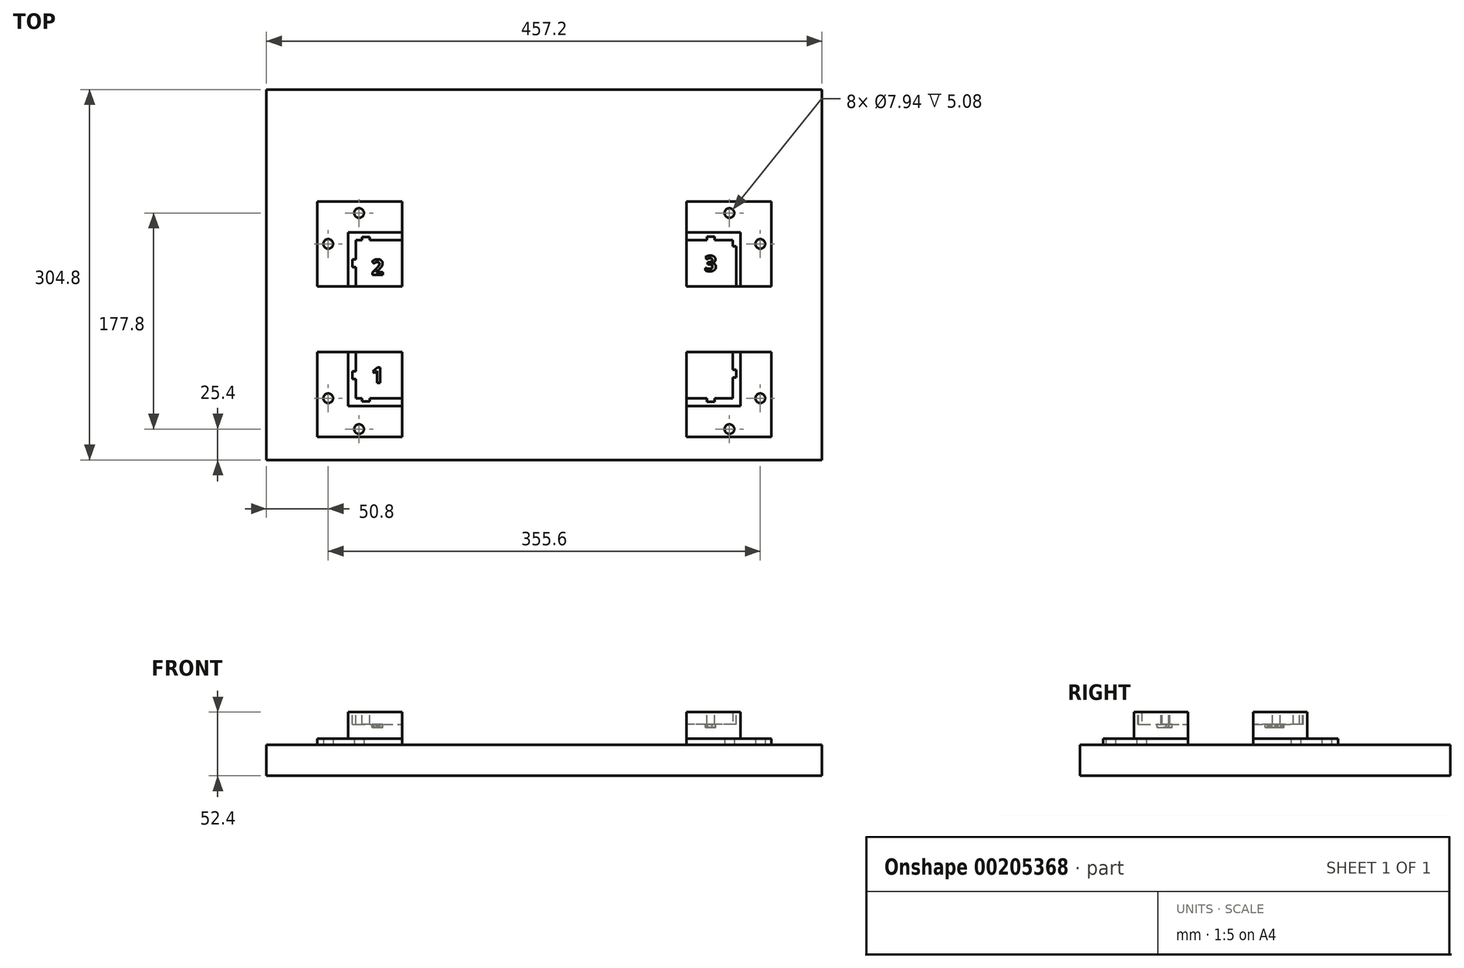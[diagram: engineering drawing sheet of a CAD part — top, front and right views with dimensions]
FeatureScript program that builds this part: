
annotation { "Feature Type Name" : "Feature", "Feature Type Description" : "" }
export const myFeature = defineFeature(function(context is Context, id is Id, definition is map)
    precondition{}
    {
        {
            var Q0;
            Q0=qCreatedBy(makeId("Top.planeOp"),FACE);
            var sketch = newSketch(context, id + "F0", { "sketchPlane" : qUnion([Q0])});
            skLineSegment(sketch, "E0.bottom", {"start": v(228.6, 152.4) * mm, "end": v(-228.6, 152.4) * mm});
            skLineSegment(sketch, "E0.top", {"start": v(228.6, -152.4) * mm, "end": v(-228.6, -152.4) * mm});
            skLineSegment(sketch, "E0.left", {"start": v(228.6, 152.4) * mm, "end": v(228.6, -152.4) * mm});
            skLineSegment(sketch, "E0.right", {"start": v(-228.6, 152.4) * mm, "end": v(-228.6, -152.4) * mm});
            skPoint(sketch, "E0.middle", {"position": v(0, 0) * mm});
            skPoint(sketch, "E1", {"position": v(-203.2, 127) * mm});
            skPoint(sketch, "E2.0.1.0", {"position": v(-203.2, 101.6) * mm});
            skPoint(sketch, "E2.0.2.0", {"position": v(-203.2, 76.2) * mm});
            skPoint(sketch, "E2.0.3.0", {"position": v(-203.2, 50.8) * mm});
            skPoint(sketch, "E2.0.4.0", {"position": v(-203.2, 25.4) * mm});
            skPoint(sketch, "E2.0.5.0", {"position": v(-203.2, 0) * mm});
            skPoint(sketch, "E2.0.6.0", {"position": v(-203.2, -25.4) * mm});
            skPoint(sketch, "E2.0.7.0", {"position": v(-203.2, -50.8) * mm});
            skPoint(sketch, "E2.0.8.0", {"position": v(-203.2, -76.2) * mm});
            skPoint(sketch, "E2.0.9.0", {"position": v(-203.2, -101.6) * mm});
            skPoint(sketch, "E2.0.10.0", {"position": v(-203.2, -127) * mm});
            skPoint(sketch, "E2.1.0.0", {"position": v(-177.8, 127) * mm});
            skPoint(sketch, "E2.1.1.0", {"position": v(-177.8, 101.6) * mm});
            skPoint(sketch, "E2.1.2.0", {"position": v(-177.8, 76.2) * mm});
            skPoint(sketch, "E2.1.3.0", {"position": v(-177.8, 50.8) * mm});
            skPoint(sketch, "E2.1.4.0", {"position": v(-177.8, 25.4) * mm});
            skPoint(sketch, "E2.1.5.0", {"position": v(-177.8, 0) * mm});
            skPoint(sketch, "E2.1.6.0", {"position": v(-177.8, -25.4) * mm});
            skPoint(sketch, "E2.1.7.0", {"position": v(-177.8, -50.8) * mm});
            skPoint(sketch, "E2.1.8.0", {"position": v(-177.8, -76.2) * mm});
            skPoint(sketch, "E2.1.9.0", {"position": v(-177.8, -101.6) * mm});
            skPoint(sketch, "E2.1.10.0", {"position": v(-177.8, -127) * mm});
            skPoint(sketch, "E2.2.0.0", {"position": v(-152.4, 127) * mm});
            skPoint(sketch, "E2.2.1.0", {"position": v(-152.4, 101.6) * mm});
            skPoint(sketch, "E2.2.2.0", {"position": v(-152.4, 76.2) * mm});
            skPoint(sketch, "E2.2.3.0", {"position": v(-152.4, 50.8) * mm});
            skPoint(sketch, "E2.2.4.0", {"position": v(-152.4, 25.4) * mm});
            skPoint(sketch, "E2.2.5.0", {"position": v(-152.4, 0) * mm});
            skPoint(sketch, "E2.2.6.0", {"position": v(-152.4, -25.4) * mm});
            skPoint(sketch, "E2.2.7.0", {"position": v(-152.4, -50.8) * mm});
            skPoint(sketch, "E2.2.8.0", {"position": v(-152.4, -76.2) * mm});
            skPoint(sketch, "E2.2.9.0", {"position": v(-152.4, -101.6) * mm});
            skPoint(sketch, "E2.2.10.0", {"position": v(-152.4, -127) * mm});
            skPoint(sketch, "E2.3.0.0", {"position": v(-127, 127) * mm});
            skPoint(sketch, "E2.3.1.0", {"position": v(-127, 101.6) * mm});
            skPoint(sketch, "E2.3.2.0", {"position": v(-127, 76.2) * mm});
            skPoint(sketch, "E2.3.3.0", {"position": v(-127, 50.8) * mm});
            skPoint(sketch, "E2.3.4.0", {"position": v(-127, 25.4) * mm});
            skPoint(sketch, "E2.3.5.0", {"position": v(-127, 0) * mm});
            skPoint(sketch, "E2.3.6.0", {"position": v(-127, -25.4) * mm});
            skPoint(sketch, "E2.3.7.0", {"position": v(-127, -50.8) * mm});
            skPoint(sketch, "E2.3.8.0", {"position": v(-127, -76.2) * mm});
            skPoint(sketch, "E2.3.9.0", {"position": v(-127, -101.6) * mm});
            skPoint(sketch, "E2.3.10.0", {"position": v(-127, -127) * mm});
            skPoint(sketch, "E2.4.0.0", {"position": v(-101.6, 127) * mm});
            skPoint(sketch, "E2.4.1.0", {"position": v(-101.6, 101.6) * mm});
            skPoint(sketch, "E2.4.2.0", {"position": v(-101.6, 76.2) * mm});
            skPoint(sketch, "E2.4.3.0", {"position": v(-101.6, 50.8) * mm});
            skPoint(sketch, "E2.4.4.0", {"position": v(-101.6, 25.4) * mm});
            skPoint(sketch, "E2.4.5.0", {"position": v(-101.6, 0) * mm});
            skPoint(sketch, "E2.4.6.0", {"position": v(-101.6, -25.4) * mm});
            skPoint(sketch, "E2.4.7.0", {"position": v(-101.6, -50.8) * mm});
            skPoint(sketch, "E2.4.8.0", {"position": v(-101.6, -76.2) * mm});
            skPoint(sketch, "E2.4.9.0", {"position": v(-101.6, -101.6) * mm});
            skPoint(sketch, "E2.4.10.0", {"position": v(-101.6, -127) * mm});
            skPoint(sketch, "E2.5.0.0", {"position": v(-76.2, 127) * mm});
            skPoint(sketch, "E2.5.1.0", {"position": v(-76.2, 101.6) * mm});
            skPoint(sketch, "E2.5.2.0", {"position": v(-76.2, 76.2) * mm});
            skPoint(sketch, "E2.5.3.0", {"position": v(-76.2, 50.8) * mm});
            skPoint(sketch, "E2.5.4.0", {"position": v(-76.2, 25.4) * mm});
            skPoint(sketch, "E2.5.5.0", {"position": v(-76.2, 0) * mm});
            skPoint(sketch, "E2.5.6.0", {"position": v(-76.2, -25.4) * mm});
            skPoint(sketch, "E2.5.7.0", {"position": v(-76.2, -50.8) * mm});
            skPoint(sketch, "E2.5.8.0", {"position": v(-76.2, -76.2) * mm});
            skPoint(sketch, "E2.5.9.0", {"position": v(-76.2, -101.6) * mm});
            skPoint(sketch, "E2.5.10.0", {"position": v(-76.2, -127) * mm});
            skPoint(sketch, "E2.6.0.0", {"position": v(-50.8, 127) * mm});
            skPoint(sketch, "E2.6.1.0", {"position": v(-50.8, 101.6) * mm});
            skPoint(sketch, "E2.6.2.0", {"position": v(-50.8, 76.2) * mm});
            skPoint(sketch, "E2.6.3.0", {"position": v(-50.8, 50.8) * mm});
            skPoint(sketch, "E2.6.4.0", {"position": v(-50.8, 25.4) * mm});
            skPoint(sketch, "E2.6.5.0", {"position": v(-50.8, 0) * mm});
            skPoint(sketch, "E2.6.6.0", {"position": v(-50.8, -25.4) * mm});
            skPoint(sketch, "E2.6.7.0", {"position": v(-50.8, -50.8) * mm});
            skPoint(sketch, "E2.6.8.0", {"position": v(-50.8, -76.2) * mm});
            skPoint(sketch, "E2.6.9.0", {"position": v(-50.8, -101.6) * mm});
            skPoint(sketch, "E2.6.10.0", {"position": v(-50.8, -127) * mm});
            skPoint(sketch, "E2.7.0.0", {"position": v(-25.4, 127) * mm});
            skPoint(sketch, "E2.7.1.0", {"position": v(-25.4, 101.6) * mm});
            skPoint(sketch, "E2.7.2.0", {"position": v(-25.4, 76.2) * mm});
            skPoint(sketch, "E2.7.3.0", {"position": v(-25.4, 50.8) * mm});
            skPoint(sketch, "E2.7.4.0", {"position": v(-25.4, 25.4) * mm});
            skPoint(sketch, "E2.7.5.0", {"position": v(-25.4, 0) * mm});
            skPoint(sketch, "E2.7.6.0", {"position": v(-25.4, -25.4) * mm});
            skPoint(sketch, "E2.7.7.0", {"position": v(-25.4, -50.8) * mm});
            skPoint(sketch, "E2.7.8.0", {"position": v(-25.4, -76.2) * mm});
            skPoint(sketch, "E2.7.9.0", {"position": v(-25.4, -101.6) * mm});
            skPoint(sketch, "E2.7.10.0", {"position": v(-25.4, -127) * mm});
            skPoint(sketch, "E2.8.0.0", {"position": v(0, 127) * mm});
            skPoint(sketch, "E2.8.1.0", {"position": v(0, 101.6) * mm});
            skPoint(sketch, "E2.8.2.0", {"position": v(0, 76.2) * mm});
            skPoint(sketch, "E2.8.3.0", {"position": v(0, 50.8) * mm});
            skPoint(sketch, "E2.8.4.0", {"position": v(0, 25.4) * mm});
            skPoint(sketch, "E2.8.6.0", {"position": v(0, -25.4) * mm});
            skPoint(sketch, "E2.8.7.0", {"position": v(0, -50.8) * mm});
            skPoint(sketch, "E2.8.8.0", {"position": v(0, -76.2) * mm});
            skPoint(sketch, "E2.8.9.0", {"position": v(0, -101.6) * mm});
            skPoint(sketch, "E2.8.10.0", {"position": v(0, -127) * mm});
            skPoint(sketch, "E2.9.0.0", {"position": v(25.4, 127) * mm});
            skPoint(sketch, "E2.9.1.0", {"position": v(25.4, 101.6) * mm});
            skPoint(sketch, "E2.9.2.0", {"position": v(25.4, 76.2) * mm});
            skPoint(sketch, "E2.9.3.0", {"position": v(25.4, 50.8) * mm});
            skPoint(sketch, "E2.9.4.0", {"position": v(25.4, 25.4) * mm});
            skPoint(sketch, "E2.9.5.0", {"position": v(25.4, 0) * mm});
            skPoint(sketch, "E2.9.6.0", {"position": v(25.4, -25.4) * mm});
            skPoint(sketch, "E2.9.7.0", {"position": v(25.4, -50.8) * mm});
            skPoint(sketch, "E2.9.8.0", {"position": v(25.4, -76.2) * mm});
            skPoint(sketch, "E2.9.9.0", {"position": v(25.4, -101.6) * mm});
            skPoint(sketch, "E2.9.10.0", {"position": v(25.4, -127) * mm});
            skPoint(sketch, "E2.10.0.0", {"position": v(50.8, 127) * mm});
            skPoint(sketch, "E2.10.1.0", {"position": v(50.8, 101.6) * mm});
            skPoint(sketch, "E2.10.2.0", {"position": v(50.8, 76.2) * mm});
            skPoint(sketch, "E2.10.3.0", {"position": v(50.8, 50.8) * mm});
            skPoint(sketch, "E2.10.4.0", {"position": v(50.8, 25.4) * mm});
            skPoint(sketch, "E2.10.5.0", {"position": v(50.8, 0) * mm});
            skPoint(sketch, "E2.10.6.0", {"position": v(50.8, -25.4) * mm});
            skPoint(sketch, "E2.10.7.0", {"position": v(50.8, -50.8) * mm});
            skPoint(sketch, "E2.10.8.0", {"position": v(50.8, -76.2) * mm});
            skPoint(sketch, "E2.10.9.0", {"position": v(50.8, -101.6) * mm});
            skPoint(sketch, "E2.10.10.0", {"position": v(50.8, -127) * mm});
            skPoint(sketch, "E2.11.0.0", {"position": v(76.2, 127) * mm});
            skPoint(sketch, "E2.11.1.0", {"position": v(76.2, 101.6) * mm});
            skPoint(sketch, "E2.11.2.0", {"position": v(76.2, 76.2) * mm});
            skPoint(sketch, "E2.11.3.0", {"position": v(76.2, 50.8) * mm});
            skPoint(sketch, "E2.11.4.0", {"position": v(76.2, 25.4) * mm});
            skPoint(sketch, "E2.11.5.0", {"position": v(76.2, 0) * mm});
            skPoint(sketch, "E2.11.6.0", {"position": v(76.2, -25.4) * mm});
            skPoint(sketch, "E2.11.7.0", {"position": v(76.2, -50.8) * mm});
            skPoint(sketch, "E2.11.8.0", {"position": v(76.2, -76.2) * mm});
            skPoint(sketch, "E2.11.9.0", {"position": v(76.2, -101.6) * mm});
            skPoint(sketch, "E2.11.10.0", {"position": v(76.2, -127) * mm});
            skPoint(sketch, "E2.12.0.0", {"position": v(101.6, 127) * mm});
            skPoint(sketch, "E2.12.1.0", {"position": v(101.6, 101.6) * mm});
            skPoint(sketch, "E2.12.2.0", {"position": v(101.6, 76.2) * mm});
            skPoint(sketch, "E2.12.3.0", {"position": v(101.6, 50.8) * mm});
            skPoint(sketch, "E2.12.4.0", {"position": v(101.6, 25.4) * mm});
            skPoint(sketch, "E2.12.5.0", {"position": v(101.6, 0) * mm});
            skPoint(sketch, "E2.12.6.0", {"position": v(101.6, -25.4) * mm});
            skPoint(sketch, "E2.12.7.0", {"position": v(101.6, -50.8) * mm});
            skPoint(sketch, "E2.12.8.0", {"position": v(101.6, -76.2) * mm});
            skPoint(sketch, "E2.12.9.0", {"position": v(101.6, -101.6) * mm});
            skPoint(sketch, "E2.12.10.0", {"position": v(101.6, -127) * mm});
            skPoint(sketch, "E2.13.0.0", {"position": v(127, 127) * mm});
            skPoint(sketch, "E2.13.1.0", {"position": v(127, 101.6) * mm});
            skPoint(sketch, "E2.13.2.0", {"position": v(127, 76.2) * mm});
            skPoint(sketch, "E2.13.3.0", {"position": v(127, 50.8) * mm});
            skPoint(sketch, "E2.13.4.0", {"position": v(127, 25.4) * mm});
            skPoint(sketch, "E2.13.5.0", {"position": v(127, 0) * mm});
            skPoint(sketch, "E2.13.6.0", {"position": v(127, -25.4) * mm});
            skPoint(sketch, "E2.13.7.0", {"position": v(127, -50.8) * mm});
            skPoint(sketch, "E2.13.8.0", {"position": v(127, -76.2) * mm});
            skPoint(sketch, "E2.13.9.0", {"position": v(127, -101.6) * mm});
            skPoint(sketch, "E2.13.10.0", {"position": v(127, -127) * mm});
            skPoint(sketch, "E2.14.0.0", {"position": v(152.4, 127) * mm});
            skPoint(sketch, "E2.14.1.0", {"position": v(152.4, 101.6) * mm});
            skPoint(sketch, "E2.14.2.0", {"position": v(152.4, 76.2) * mm});
            skPoint(sketch, "E2.14.3.0", {"position": v(152.4, 50.8) * mm});
            skPoint(sketch, "E2.14.4.0", {"position": v(152.4, 25.4) * mm});
            skPoint(sketch, "E2.14.5.0", {"position": v(152.4, 0) * mm});
            skPoint(sketch, "E2.14.6.0", {"position": v(152.4, -25.4) * mm});
            skPoint(sketch, "E2.14.7.0", {"position": v(152.4, -50.8) * mm});
            skPoint(sketch, "E2.14.8.0", {"position": v(152.4, -76.2) * mm});
            skPoint(sketch, "E2.14.9.0", {"position": v(152.4, -101.6) * mm});
            skPoint(sketch, "E2.14.10.0", {"position": v(152.4, -127) * mm});
            skPoint(sketch, "E2.15.0.0", {"position": v(177.8, 127) * mm});
            skPoint(sketch, "E2.15.1.0", {"position": v(177.8, 101.6) * mm});
            skPoint(sketch, "E2.15.2.0", {"position": v(177.8, 76.2) * mm});
            skPoint(sketch, "E2.15.3.0", {"position": v(177.8, 50.8) * mm});
            skPoint(sketch, "E2.15.4.0", {"position": v(177.8, 25.4) * mm});
            skPoint(sketch, "E2.15.5.0", {"position": v(177.8, 0) * mm});
            skPoint(sketch, "E2.15.6.0", {"position": v(177.8, -25.4) * mm});
            skPoint(sketch, "E2.15.7.0", {"position": v(177.8, -50.8) * mm});
            skPoint(sketch, "E2.15.8.0", {"position": v(177.8, -76.2) * mm});
            skPoint(sketch, "E2.15.9.0", {"position": v(177.8, -101.6) * mm});
            skPoint(sketch, "E2.15.10.0", {"position": v(177.8, -127) * mm});
            skPoint(sketch, "E2.16.0.0", {"position": v(203.2, 127) * mm});
            skPoint(sketch, "E2.16.1.0", {"position": v(203.2, 101.6) * mm});
            skPoint(sketch, "E2.16.2.0", {"position": v(203.2, 76.2) * mm});
            skPoint(sketch, "E2.16.3.0", {"position": v(203.2, 50.8) * mm});
            skPoint(sketch, "E2.16.4.0", {"position": v(203.2, 25.4) * mm});
            skPoint(sketch, "E2.16.5.0", {"position": v(203.2, 0) * mm});
            skPoint(sketch, "E2.16.6.0", {"position": v(203.2, -25.4) * mm});
            skPoint(sketch, "E2.16.7.0", {"position": v(203.2, -50.8) * mm});
            skPoint(sketch, "E2.16.8.0", {"position": v(203.2, -76.2) * mm});
            skPoint(sketch, "E2.16.9.0", {"position": v(203.2, -101.6) * mm});
            skPoint(sketch, "E2.16.10.0", {"position": v(203.2, -127) * mm});
            skLineSegment(sketch, "E2.direction1", {"start": v(-203.2, 127) * mm, "end": v(-177.8, 127) * mm, "construction": true});
            skLineSegment(sketch, "E2.direction2", {"start": v(-203.2, 127) * mm, "end": v(-203.2, 101.6) * mm, "construction": true});
            skCircle(sketch, "E3", {"center": v(-203.2, 127) * mm, "radius": 3.18 * mm, "construction": true});
            skCircle(sketch, "E4.0.1.0", {"center": v(-203.2, 101.6) * mm, "radius": 3.18 * mm, "construction": true});
            skCircle(sketch, "E4.0.2.0", {"center": v(-203.2, 76.2) * mm, "radius": 3.18 * mm, "construction": true});
            skCircle(sketch, "E4.0.3.0", {"center": v(-203.2, 50.8) * mm, "radius": 3.18 * mm, "construction": true});
            skCircle(sketch, "E4.0.4.0", {"center": v(-203.2, 25.4) * mm, "radius": 3.18 * mm, "construction": true});
            skCircle(sketch, "E4.0.5.0", {"center": v(-203.2, 0) * mm, "radius": 3.18 * mm, "construction": true});
            skCircle(sketch, "E4.0.6.0", {"center": v(-203.2, -25.4) * mm, "radius": 3.18 * mm, "construction": true});
            skCircle(sketch, "E4.0.7.0", {"center": v(-203.2, -50.8) * mm, "radius": 3.18 * mm, "construction": true});
            skCircle(sketch, "E4.0.8.0", {"center": v(-203.2, -76.2) * mm, "radius": 3.18 * mm, "construction": true});
            skCircle(sketch, "E4.0.9.0", {"center": v(-203.2, -101.6) * mm, "radius": 3.18 * mm, "construction": true});
            skCircle(sketch, "E4.0.10.0", {"center": v(-203.2, -127) * mm, "radius": 3.18 * mm, "construction": true});
            skCircle(sketch, "E4.1.0.0", {"center": v(-177.8, 127) * mm, "radius": 3.18 * mm, "construction": true});
            skCircle(sketch, "E4.1.1.0", {"center": v(-177.8, 101.6) * mm, "radius": 3.18 * mm, "construction": true});
            skCircle(sketch, "E4.1.2.0", {"center": v(-177.8, 76.2) * mm, "radius": 3.18 * mm, "construction": true});
            skCircle(sketch, "E4.1.3.0", {"center": v(-177.8, 50.8) * mm, "radius": 3.18 * mm, "construction": true});
            skCircle(sketch, "E4.1.4.0", {"center": v(-177.8, 25.4) * mm, "radius": 3.18 * mm, "construction": true});
            skCircle(sketch, "E4.1.5.0", {"center": v(-177.8, 0) * mm, "radius": 3.18 * mm, "construction": true});
            skCircle(sketch, "E4.1.6.0", {"center": v(-177.8, -25.4) * mm, "radius": 3.18 * mm, "construction": true});
            skCircle(sketch, "E4.1.7.0", {"center": v(-177.8, -50.8) * mm, "radius": 3.18 * mm, "construction": true});
            skCircle(sketch, "E4.1.8.0", {"center": v(-177.8, -76.2) * mm, "radius": 3.18 * mm, "construction": true});
            skCircle(sketch, "E4.1.9.0", {"center": v(-177.8, -101.6) * mm, "radius": 3.18 * mm, "construction": true});
            skCircle(sketch, "E4.1.10.0", {"center": v(-177.8, -127) * mm, "radius": 3.18 * mm, "construction": true});
            skCircle(sketch, "E4.2.0.0", {"center": v(-152.4, 127) * mm, "radius": 3.18 * mm, "construction": true});
            skCircle(sketch, "E4.2.1.0", {"center": v(-152.4, 101.6) * mm, "radius": 3.18 * mm, "construction": true});
            skCircle(sketch, "E4.2.2.0", {"center": v(-152.4, 76.2) * mm, "radius": 3.18 * mm, "construction": true});
            skCircle(sketch, "E4.2.3.0", {"center": v(-152.4, 50.8) * mm, "radius": 3.18 * mm, "construction": true});
            skCircle(sketch, "E4.2.4.0", {"center": v(-152.4, 25.4) * mm, "radius": 3.18 * mm, "construction": true});
            skCircle(sketch, "E4.2.5.0", {"center": v(-152.4, 0) * mm, "radius": 3.18 * mm, "construction": true});
            skCircle(sketch, "E4.2.6.0", {"center": v(-152.4, -25.4) * mm, "radius": 3.18 * mm, "construction": true});
            skCircle(sketch, "E4.2.7.0", {"center": v(-152.4, -50.8) * mm, "radius": 3.18 * mm, "construction": true});
            skCircle(sketch, "E4.2.8.0", {"center": v(-152.4, -76.2) * mm, "radius": 3.18 * mm, "construction": true});
            skCircle(sketch, "E4.2.9.0", {"center": v(-152.4, -101.6) * mm, "radius": 3.18 * mm, "construction": true});
            skCircle(sketch, "E4.2.10.0", {"center": v(-152.4, -127) * mm, "radius": 3.18 * mm, "construction": true});
            skCircle(sketch, "E4.3.0.0", {"center": v(-127, 127) * mm, "radius": 3.18 * mm, "construction": true});
            skCircle(sketch, "E4.3.1.0", {"center": v(-127, 101.6) * mm, "radius": 3.18 * mm, "construction": true});
            skCircle(sketch, "E4.3.2.0", {"center": v(-127, 76.2) * mm, "radius": 3.18 * mm, "construction": true});
            skCircle(sketch, "E4.3.3.0", {"center": v(-127, 50.8) * mm, "radius": 3.18 * mm, "construction": true});
            skCircle(sketch, "E4.3.4.0", {"center": v(-127, 25.4) * mm, "radius": 3.18 * mm, "construction": true});
            skCircle(sketch, "E4.3.5.0", {"center": v(-127, 0) * mm, "radius": 3.18 * mm, "construction": true});
            skCircle(sketch, "E4.3.6.0", {"center": v(-127, -25.4) * mm, "radius": 3.18 * mm, "construction": true});
            skCircle(sketch, "E4.3.7.0", {"center": v(-127, -50.8) * mm, "radius": 3.18 * mm, "construction": true});
            skCircle(sketch, "E4.3.8.0", {"center": v(-127, -76.2) * mm, "radius": 3.18 * mm, "construction": true});
            skCircle(sketch, "E4.3.9.0", {"center": v(-127, -101.6) * mm, "radius": 3.18 * mm, "construction": true});
            skCircle(sketch, "E4.3.10.0", {"center": v(-127, -127) * mm, "radius": 3.18 * mm, "construction": true});
            skCircle(sketch, "E4.4.0.0", {"center": v(-101.6, 127) * mm, "radius": 3.18 * mm, "construction": true});
            skCircle(sketch, "E4.4.1.0", {"center": v(-101.6, 101.6) * mm, "radius": 3.18 * mm, "construction": true});
            skCircle(sketch, "E4.4.2.0", {"center": v(-101.6, 76.2) * mm, "radius": 3.18 * mm, "construction": true});
            skCircle(sketch, "E4.4.3.0", {"center": v(-101.6, 50.8) * mm, "radius": 3.18 * mm, "construction": true});
            skCircle(sketch, "E4.4.4.0", {"center": v(-101.6, 25.4) * mm, "radius": 3.18 * mm, "construction": true});
            skCircle(sketch, "E4.4.5.0", {"center": v(-101.6, 0) * mm, "radius": 3.18 * mm, "construction": true});
            skCircle(sketch, "E4.4.6.0", {"center": v(-101.6, -25.4) * mm, "radius": 3.18 * mm, "construction": true});
            skCircle(sketch, "E4.4.7.0", {"center": v(-101.6, -50.8) * mm, "radius": 3.18 * mm, "construction": true});
            skCircle(sketch, "E4.4.8.0", {"center": v(-101.6, -76.2) * mm, "radius": 3.18 * mm, "construction": true});
            skCircle(sketch, "E4.4.9.0", {"center": v(-101.6, -101.6) * mm, "radius": 3.18 * mm, "construction": true});
            skCircle(sketch, "E4.4.10.0", {"center": v(-101.6, -127) * mm, "radius": 3.18 * mm, "construction": true});
            skCircle(sketch, "E4.5.0.0", {"center": v(-76.2, 127) * mm, "radius": 3.18 * mm, "construction": true});
            skCircle(sketch, "E4.5.1.0", {"center": v(-76.2, 101.6) * mm, "radius": 3.18 * mm, "construction": true});
            skCircle(sketch, "E4.5.2.0", {"center": v(-76.2, 76.2) * mm, "radius": 3.18 * mm, "construction": true});
            skCircle(sketch, "E4.5.3.0", {"center": v(-76.2, 50.8) * mm, "radius": 3.18 * mm, "construction": true});
            skCircle(sketch, "E4.5.4.0", {"center": v(-76.2, 25.4) * mm, "radius": 3.18 * mm, "construction": true});
            skCircle(sketch, "E4.5.5.0", {"center": v(-76.2, 0) * mm, "radius": 3.18 * mm, "construction": true});
            skCircle(sketch, "E4.5.6.0", {"center": v(-76.2, -25.4) * mm, "radius": 3.18 * mm, "construction": true});
            skCircle(sketch, "E4.5.7.0", {"center": v(-76.2, -50.8) * mm, "radius": 3.18 * mm, "construction": true});
            skCircle(sketch, "E4.5.8.0", {"center": v(-76.2, -76.2) * mm, "radius": 3.18 * mm, "construction": true});
            skCircle(sketch, "E4.5.9.0", {"center": v(-76.2, -101.6) * mm, "radius": 3.18 * mm, "construction": true});
            skCircle(sketch, "E4.5.10.0", {"center": v(-76.2, -127) * mm, "radius": 3.18 * mm, "construction": true});
            skCircle(sketch, "E4.6.0.0", {"center": v(-50.8, 127) * mm, "radius": 3.18 * mm, "construction": true});
            skCircle(sketch, "E4.6.1.0", {"center": v(-50.8, 101.6) * mm, "radius": 3.18 * mm, "construction": true});
            skCircle(sketch, "E4.6.2.0", {"center": v(-50.8, 76.2) * mm, "radius": 3.18 * mm, "construction": true});
            skCircle(sketch, "E4.6.3.0", {"center": v(-50.8, 50.8) * mm, "radius": 3.18 * mm, "construction": true});
            skCircle(sketch, "E4.6.4.0", {"center": v(-50.8, 25.4) * mm, "radius": 3.18 * mm, "construction": true});
            skCircle(sketch, "E4.6.5.0", {"center": v(-50.8, 0) * mm, "radius": 3.18 * mm, "construction": true});
            skCircle(sketch, "E4.6.6.0", {"center": v(-50.8, -25.4) * mm, "radius": 3.18 * mm, "construction": true});
            skCircle(sketch, "E4.6.7.0", {"center": v(-50.8, -50.8) * mm, "radius": 3.18 * mm, "construction": true});
            skCircle(sketch, "E4.6.8.0", {"center": v(-50.8, -76.2) * mm, "radius": 3.18 * mm, "construction": true});
            skCircle(sketch, "E4.6.9.0", {"center": v(-50.8, -101.6) * mm, "radius": 3.18 * mm, "construction": true});
            skCircle(sketch, "E4.6.10.0", {"center": v(-50.8, -127) * mm, "radius": 3.18 * mm, "construction": true});
            skCircle(sketch, "E4.7.0.0", {"center": v(-25.4, 127) * mm, "radius": 3.18 * mm, "construction": true});
            skCircle(sketch, "E4.7.1.0", {"center": v(-25.4, 101.6) * mm, "radius": 3.18 * mm, "construction": true});
            skCircle(sketch, "E4.7.2.0", {"center": v(-25.4, 76.2) * mm, "radius": 3.18 * mm, "construction": true});
            skCircle(sketch, "E4.7.3.0", {"center": v(-25.4, 50.8) * mm, "radius": 3.18 * mm, "construction": true});
            skCircle(sketch, "E4.7.4.0", {"center": v(-25.4, 25.4) * mm, "radius": 3.18 * mm, "construction": true});
            skCircle(sketch, "E4.7.5.0", {"center": v(-25.4, 0) * mm, "radius": 3.18 * mm, "construction": true});
            skCircle(sketch, "E4.7.6.0", {"center": v(-25.4, -25.4) * mm, "radius": 3.18 * mm, "construction": true});
            skCircle(sketch, "E4.7.7.0", {"center": v(-25.4, -50.8) * mm, "radius": 3.18 * mm, "construction": true});
            skCircle(sketch, "E4.7.8.0", {"center": v(-25.4, -76.2) * mm, "radius": 3.18 * mm, "construction": true});
            skCircle(sketch, "E4.7.9.0", {"center": v(-25.4, -101.6) * mm, "radius": 3.18 * mm, "construction": true});
            skCircle(sketch, "E4.7.10.0", {"center": v(-25.4, -127) * mm, "radius": 3.18 * mm, "construction": true});
            skCircle(sketch, "E4.8.0.0", {"center": v(0, 127) * mm, "radius": 3.18 * mm, "construction": true});
            skCircle(sketch, "E4.8.1.0", {"center": v(0, 101.6) * mm, "radius": 3.18 * mm, "construction": true});
            skCircle(sketch, "E4.8.2.0", {"center": v(0, 76.2) * mm, "radius": 3.18 * mm, "construction": true});
            skCircle(sketch, "E4.8.3.0", {"center": v(0, 50.8) * mm, "radius": 3.18 * mm, "construction": true});
            skCircle(sketch, "E4.8.4.0", {"center": v(0, 25.4) * mm, "radius": 3.18 * mm, "construction": true});
            skCircle(sketch, "E4.8.5.0", {"center": v(0, 0) * mm, "radius": 3.18 * mm, "construction": true});
            skCircle(sketch, "E4.8.6.0", {"center": v(0, -25.4) * mm, "radius": 3.18 * mm, "construction": true});
            skCircle(sketch, "E4.8.7.0", {"center": v(0, -50.8) * mm, "radius": 3.18 * mm, "construction": true});
            skCircle(sketch, "E4.8.8.0", {"center": v(0, -76.2) * mm, "radius": 3.18 * mm, "construction": true});
            skCircle(sketch, "E4.8.9.0", {"center": v(0, -101.6) * mm, "radius": 3.18 * mm, "construction": true});
            skCircle(sketch, "E4.8.10.0", {"center": v(0, -127) * mm, "radius": 3.18 * mm, "construction": true});
            skCircle(sketch, "E4.9.0.0", {"center": v(25.4, 127) * mm, "radius": 3.18 * mm, "construction": true});
            skCircle(sketch, "E4.9.1.0", {"center": v(25.4, 101.6) * mm, "radius": 3.18 * mm, "construction": true});
            skCircle(sketch, "E4.9.2.0", {"center": v(25.4, 76.2) * mm, "radius": 3.18 * mm, "construction": true});
            skCircle(sketch, "E4.9.3.0", {"center": v(25.4, 50.8) * mm, "radius": 3.18 * mm, "construction": true});
            skCircle(sketch, "E4.9.4.0", {"center": v(25.4, 25.4) * mm, "radius": 3.18 * mm, "construction": true});
            skCircle(sketch, "E4.9.5.0", {"center": v(25.4, 0) * mm, "radius": 3.18 * mm, "construction": true});
            skCircle(sketch, "E4.9.6.0", {"center": v(25.4, -25.4) * mm, "radius": 3.18 * mm, "construction": true});
            skCircle(sketch, "E4.9.7.0", {"center": v(25.4, -50.8) * mm, "radius": 3.18 * mm, "construction": true});
            skCircle(sketch, "E4.9.8.0", {"center": v(25.4, -76.2) * mm, "radius": 3.18 * mm, "construction": true});
            skCircle(sketch, "E4.9.9.0", {"center": v(25.4, -101.6) * mm, "radius": 3.18 * mm, "construction": true});
            skCircle(sketch, "E4.9.10.0", {"center": v(25.4, -127) * mm, "radius": 3.18 * mm, "construction": true});
            skCircle(sketch, "E4.10.0.0", {"center": v(50.8, 127) * mm, "radius": 3.18 * mm, "construction": true});
            skCircle(sketch, "E4.10.1.0", {"center": v(50.8, 101.6) * mm, "radius": 3.18 * mm, "construction": true});
            skCircle(sketch, "E4.10.2.0", {"center": v(50.8, 76.2) * mm, "radius": 3.18 * mm, "construction": true});
            skCircle(sketch, "E4.10.3.0", {"center": v(50.8, 50.8) * mm, "radius": 3.18 * mm, "construction": true});
            skCircle(sketch, "E4.10.4.0", {"center": v(50.8, 25.4) * mm, "radius": 3.18 * mm, "construction": true});
            skCircle(sketch, "E4.10.5.0", {"center": v(50.8, 0) * mm, "radius": 3.18 * mm, "construction": true});
            skCircle(sketch, "E4.10.6.0", {"center": v(50.8, -25.4) * mm, "radius": 3.18 * mm, "construction": true});
            skCircle(sketch, "E4.10.7.0", {"center": v(50.8, -50.8) * mm, "radius": 3.18 * mm, "construction": true});
            skCircle(sketch, "E4.10.8.0", {"center": v(50.8, -76.2) * mm, "radius": 3.18 * mm, "construction": true});
            skCircle(sketch, "E4.10.9.0", {"center": v(50.8, -101.6) * mm, "radius": 3.18 * mm, "construction": true});
            skCircle(sketch, "E4.10.10.0", {"center": v(50.8, -127) * mm, "radius": 3.18 * mm, "construction": true});
            skCircle(sketch, "E4.11.0.0", {"center": v(76.2, 127) * mm, "radius": 3.18 * mm, "construction": true});
            skCircle(sketch, "E4.11.1.0", {"center": v(76.2, 101.6) * mm, "radius": 3.18 * mm, "construction": true});
            skCircle(sketch, "E4.11.2.0", {"center": v(76.2, 76.2) * mm, "radius": 3.18 * mm, "construction": true});
            skCircle(sketch, "E4.11.3.0", {"center": v(76.2, 50.8) * mm, "radius": 3.18 * mm, "construction": true});
            skCircle(sketch, "E4.11.4.0", {"center": v(76.2, 25.4) * mm, "radius": 3.18 * mm, "construction": true});
            skCircle(sketch, "E4.11.5.0", {"center": v(76.2, 0) * mm, "radius": 3.18 * mm, "construction": true});
            skCircle(sketch, "E4.11.6.0", {"center": v(76.2, -25.4) * mm, "radius": 3.18 * mm, "construction": true});
            skCircle(sketch, "E4.11.7.0", {"center": v(76.2, -50.8) * mm, "radius": 3.18 * mm, "construction": true});
            skCircle(sketch, "E4.11.8.0", {"center": v(76.2, -76.2) * mm, "radius": 3.18 * mm, "construction": true});
            skCircle(sketch, "E4.11.9.0", {"center": v(76.2, -101.6) * mm, "radius": 3.18 * mm, "construction": true});
            skCircle(sketch, "E4.11.10.0", {"center": v(76.2, -127) * mm, "radius": 3.18 * mm, "construction": true});
            skCircle(sketch, "E4.12.0.0", {"center": v(101.6, 127) * mm, "radius": 3.18 * mm, "construction": true});
            skCircle(sketch, "E4.12.1.0", {"center": v(101.6, 101.6) * mm, "radius": 3.18 * mm, "construction": true});
            skCircle(sketch, "E4.12.2.0", {"center": v(101.6, 76.2) * mm, "radius": 3.18 * mm, "construction": true});
            skCircle(sketch, "E4.12.3.0", {"center": v(101.6, 50.8) * mm, "radius": 3.18 * mm, "construction": true});
            skCircle(sketch, "E4.12.4.0", {"center": v(101.6, 25.4) * mm, "radius": 3.18 * mm, "construction": true});
            skCircle(sketch, "E4.12.5.0", {"center": v(101.6, 0) * mm, "radius": 3.18 * mm, "construction": true});
            skCircle(sketch, "E4.12.6.0", {"center": v(101.6, -25.4) * mm, "radius": 3.18 * mm, "construction": true});
            skCircle(sketch, "E4.12.7.0", {"center": v(101.6, -50.8) * mm, "radius": 3.18 * mm, "construction": true});
            skCircle(sketch, "E4.12.8.0", {"center": v(101.6, -76.2) * mm, "radius": 3.18 * mm, "construction": true});
            skCircle(sketch, "E4.12.9.0", {"center": v(101.6, -101.6) * mm, "radius": 3.18 * mm, "construction": true});
            skCircle(sketch, "E4.12.10.0", {"center": v(101.6, -127) * mm, "radius": 3.18 * mm, "construction": true});
            skCircle(sketch, "E4.13.0.0", {"center": v(127, 127) * mm, "radius": 3.18 * mm, "construction": true});
            skCircle(sketch, "E4.13.1.0", {"center": v(127, 101.6) * mm, "radius": 3.18 * mm, "construction": true});
            skCircle(sketch, "E4.13.2.0", {"center": v(127, 76.2) * mm, "radius": 3.18 * mm, "construction": true});
            skCircle(sketch, "E4.13.3.0", {"center": v(127, 50.8) * mm, "radius": 3.18 * mm, "construction": true});
            skCircle(sketch, "E4.13.4.0", {"center": v(127, 25.4) * mm, "radius": 3.18 * mm, "construction": true});
            skCircle(sketch, "E4.13.5.0", {"center": v(127, 0) * mm, "radius": 3.18 * mm, "construction": true});
            skCircle(sketch, "E4.13.6.0", {"center": v(127, -25.4) * mm, "radius": 3.18 * mm, "construction": true});
            skCircle(sketch, "E4.13.7.0", {"center": v(127, -50.8) * mm, "radius": 3.18 * mm, "construction": true});
            skCircle(sketch, "E4.13.8.0", {"center": v(127, -76.2) * mm, "radius": 3.18 * mm, "construction": true});
            skCircle(sketch, "E4.13.9.0", {"center": v(127, -101.6) * mm, "radius": 3.18 * mm, "construction": true});
            skCircle(sketch, "E4.13.10.0", {"center": v(127, -127) * mm, "radius": 3.18 * mm, "construction": true});
            skCircle(sketch, "E4.14.0.0", {"center": v(152.4, 127) * mm, "radius": 3.18 * mm, "construction": true});
            skCircle(sketch, "E4.14.1.0", {"center": v(152.4, 101.6) * mm, "radius": 3.18 * mm, "construction": true});
            skCircle(sketch, "E4.14.2.0", {"center": v(152.4, 76.2) * mm, "radius": 3.18 * mm, "construction": true});
            skCircle(sketch, "E4.14.3.0", {"center": v(152.4, 50.8) * mm, "radius": 3.18 * mm, "construction": true});
            skCircle(sketch, "E4.14.4.0", {"center": v(152.4, 25.4) * mm, "radius": 3.18 * mm, "construction": true});
            skCircle(sketch, "E4.14.5.0", {"center": v(152.4, 0) * mm, "radius": 3.18 * mm, "construction": true});
            skCircle(sketch, "E4.14.6.0", {"center": v(152.4, -25.4) * mm, "radius": 3.18 * mm, "construction": true});
            skCircle(sketch, "E4.14.7.0", {"center": v(152.4, -50.8) * mm, "radius": 3.18 * mm, "construction": true});
            skCircle(sketch, "E4.14.8.0", {"center": v(152.4, -76.2) * mm, "radius": 3.18 * mm, "construction": true});
            skCircle(sketch, "E4.14.9.0", {"center": v(152.4, -101.6) * mm, "radius": 3.18 * mm, "construction": true});
            skCircle(sketch, "E4.14.10.0", {"center": v(152.4, -127) * mm, "radius": 3.18 * mm, "construction": true});
            skCircle(sketch, "E4.15.0.0", {"center": v(177.8, 127) * mm, "radius": 3.18 * mm, "construction": true});
            skCircle(sketch, "E4.15.1.0", {"center": v(177.8, 101.6) * mm, "radius": 3.18 * mm, "construction": true});
            skCircle(sketch, "E4.15.2.0", {"center": v(177.8, 76.2) * mm, "radius": 3.18 * mm, "construction": true});
            skCircle(sketch, "E4.15.3.0", {"center": v(177.8, 50.8) * mm, "radius": 3.18 * mm, "construction": true});
            skCircle(sketch, "E4.15.4.0", {"center": v(177.8, 25.4) * mm, "radius": 3.18 * mm, "construction": true});
            skCircle(sketch, "E4.15.5.0", {"center": v(177.8, 0) * mm, "radius": 3.18 * mm, "construction": true});
            skCircle(sketch, "E4.15.6.0", {"center": v(177.8, -25.4) * mm, "radius": 3.18 * mm, "construction": true});
            skCircle(sketch, "E4.15.7.0", {"center": v(177.8, -50.8) * mm, "radius": 3.18 * mm, "construction": true});
            skCircle(sketch, "E4.15.8.0", {"center": v(177.8, -76.2) * mm, "radius": 3.18 * mm, "construction": true});
            skCircle(sketch, "E4.15.9.0", {"center": v(177.8, -101.6) * mm, "radius": 3.18 * mm, "construction": true});
            skCircle(sketch, "E4.15.10.0", {"center": v(177.8, -127) * mm, "radius": 3.18 * mm, "construction": true});
            skCircle(sketch, "E4.16.0.0", {"center": v(203.2, 127) * mm, "radius": 3.18 * mm, "construction": true});
            skCircle(sketch, "E4.16.1.0", {"center": v(203.2, 101.6) * mm, "radius": 3.18 * mm, "construction": true});
            skCircle(sketch, "E4.16.2.0", {"center": v(203.2, 76.2) * mm, "radius": 3.18 * mm, "construction": true});
            skCircle(sketch, "E4.16.3.0", {"center": v(203.2, 50.8) * mm, "radius": 3.18 * mm, "construction": true});
            skCircle(sketch, "E4.16.4.0", {"center": v(203.2, 25.4) * mm, "radius": 3.18 * mm, "construction": true});
            skCircle(sketch, "E4.16.5.0", {"center": v(203.2, 0) * mm, "radius": 3.18 * mm, "construction": true});
            skCircle(sketch, "E4.16.6.0", {"center": v(203.2, -25.4) * mm, "radius": 3.18 * mm, "construction": true});
            skCircle(sketch, "E4.16.7.0", {"center": v(203.2, -50.8) * mm, "radius": 3.18 * mm, "construction": true});
            skCircle(sketch, "E4.16.8.0", {"center": v(203.2, -76.2) * mm, "radius": 3.18 * mm, "construction": true});
            skCircle(sketch, "E4.16.9.0", {"center": v(203.2, -101.6) * mm, "radius": 3.18 * mm, "construction": true});
            skCircle(sketch, "E4.16.10.0", {"center": v(203.2, -127) * mm, "radius": 3.18 * mm, "construction": true});
            skSolve(sketch);
        }
        {
            var Q0;
            Q0 = qSketchRegion(id + "F0", true);
            extrude(context, id + "F1", {"entities" : qUnion([Q0]), "depth" : 25.4 * mm});
        }
        {
            var Q0;
            Q0=makeQuery(id+"F1.opExtrude","CAP_FACE",FACE,{"disambiguationData":[OSD([sQuery(id+"F0.wireOp",EDGE,"E0.bottom"),sQuery(id+"F0.wireOp",EDGE,"E0.top"),sQuery(id+"F0.wireOp",EDGE,"E0.left"),sQuery(id+"F0.wireOp",EDGE,"E0.right"),sQuery(id+"F0.wireOp",EDGE,"E3"),sQuery(id+"F0.wireOp",EDGE,"E4.0.1.0"),sQuery(id+"F0.wireOp",EDGE,"E4.0.2.0"),sQuery(id+"F0.wireOp",EDGE,"E4.0.3.0"),sQuery(id+"F0.wireOp",EDGE,"E4.0.4.0"),sQuery(id+"F0.wireOp",EDGE,"E4.0.5.0"),sQuery(id+"F0.wireOp",EDGE,"E4.0.6.0"),sQuery(id+"F0.wireOp",EDGE,"E4.0.7.0"),sQuery(id+"F0.wireOp",EDGE,"E4.0.8.0"),sQuery(id+"F0.wireOp",EDGE,"E4.0.9.0"),sQuery(id+"F0.wireOp",EDGE,"E4.0.10.0"),sQuery(id+"F0.wireOp",EDGE,"E4.1.0.0"),sQuery(id+"F0.wireOp",EDGE,"E4.1.1.0"),sQuery(id+"F0.wireOp",EDGE,"E4.1.2.0"),sQuery(id+"F0.wireOp",EDGE,"E4.1.3.0"),sQuery(id+"F0.wireOp",EDGE,"E4.1.4.0"),sQuery(id+"F0.wireOp",EDGE,"E4.1.5.0"),sQuery(id+"F0.wireOp",EDGE,"E4.1.6.0"),sQuery(id+"F0.wireOp",EDGE,"E4.1.7.0"),sQuery(id+"F0.wireOp",EDGE,"E4.1.8.0"),sQuery(id+"F0.wireOp",EDGE,"E4.1.9.0"),sQuery(id+"F0.wireOp",EDGE,"E4.1.10.0"),sQuery(id+"F0.wireOp",EDGE,"E4.2.0.0"),sQuery(id+"F0.wireOp",EDGE,"E4.2.1.0"),sQuery(id+"F0.wireOp",EDGE,"E4.2.2.0"),sQuery(id+"F0.wireOp",EDGE,"E4.2.3.0"),sQuery(id+"F0.wireOp",EDGE,"E4.2.4.0"),sQuery(id+"F0.wireOp",EDGE,"E4.2.5.0"),sQuery(id+"F0.wireOp",EDGE,"E4.2.6.0"),sQuery(id+"F0.wireOp",EDGE,"E4.2.7.0"),sQuery(id+"F0.wireOp",EDGE,"E4.2.8.0"),sQuery(id+"F0.wireOp",EDGE,"E4.2.9.0"),sQuery(id+"F0.wireOp",EDGE,"E4.2.10.0"),sQuery(id+"F0.wireOp",EDGE,"E4.3.0.0"),sQuery(id+"F0.wireOp",EDGE,"E4.3.1.0"),sQuery(id+"F0.wireOp",EDGE,"E4.3.2.0"),sQuery(id+"F0.wireOp",EDGE,"E4.3.3.0"),sQuery(id+"F0.wireOp",EDGE,"E4.3.4.0"),sQuery(id+"F0.wireOp",EDGE,"E4.3.5.0"),sQuery(id+"F0.wireOp",EDGE,"E4.3.6.0"),sQuery(id+"F0.wireOp",EDGE,"E4.3.7.0"),sQuery(id+"F0.wireOp",EDGE,"E4.3.8.0"),sQuery(id+"F0.wireOp",EDGE,"E4.3.9.0"),sQuery(id+"F0.wireOp",EDGE,"E4.3.10.0"),sQuery(id+"F0.wireOp",EDGE,"E4.4.0.0"),sQuery(id+"F0.wireOp",EDGE,"E4.4.1.0"),sQuery(id+"F0.wireOp",EDGE,"E4.4.2.0"),sQuery(id+"F0.wireOp",EDGE,"E4.4.3.0"),sQuery(id+"F0.wireOp",EDGE,"E4.4.4.0"),sQuery(id+"F0.wireOp",EDGE,"E4.4.5.0"),sQuery(id+"F0.wireOp",EDGE,"E4.4.6.0"),sQuery(id+"F0.wireOp",EDGE,"E4.4.7.0"),sQuery(id+"F0.wireOp",EDGE,"E4.4.8.0"),sQuery(id+"F0.wireOp",EDGE,"E4.4.9.0"),sQuery(id+"F0.wireOp",EDGE,"E4.4.10.0"),sQuery(id+"F0.wireOp",EDGE,"E4.5.0.0"),sQuery(id+"F0.wireOp",EDGE,"E4.5.1.0"),sQuery(id+"F0.wireOp",EDGE,"E4.5.2.0"),sQuery(id+"F0.wireOp",EDGE,"E4.5.3.0"),sQuery(id+"F0.wireOp",EDGE,"E4.5.4.0"),sQuery(id+"F0.wireOp",EDGE,"E4.5.5.0"),sQuery(id+"F0.wireOp",EDGE,"E4.5.6.0"),sQuery(id+"F0.wireOp",EDGE,"E4.5.7.0"),sQuery(id+"F0.wireOp",EDGE,"E4.5.8.0"),sQuery(id+"F0.wireOp",EDGE,"E4.5.9.0"),sQuery(id+"F0.wireOp",EDGE,"E4.5.10.0"),sQuery(id+"F0.wireOp",EDGE,"E4.6.0.0"),sQuery(id+"F0.wireOp",EDGE,"E4.6.1.0"),sQuery(id+"F0.wireOp",EDGE,"E4.6.2.0"),sQuery(id+"F0.wireOp",EDGE,"E4.6.3.0"),sQuery(id+"F0.wireOp",EDGE,"E4.6.4.0"),sQuery(id+"F0.wireOp",EDGE,"E4.6.5.0"),sQuery(id+"F0.wireOp",EDGE,"E4.6.6.0"),sQuery(id+"F0.wireOp",EDGE,"E4.6.7.0"),sQuery(id+"F0.wireOp",EDGE,"E4.6.8.0"),sQuery(id+"F0.wireOp",EDGE,"E4.6.9.0"),sQuery(id+"F0.wireOp",EDGE,"E4.6.10.0"),sQuery(id+"F0.wireOp",EDGE,"E4.7.0.0"),sQuery(id+"F0.wireOp",EDGE,"E4.7.1.0"),sQuery(id+"F0.wireOp",EDGE,"E4.7.2.0"),sQuery(id+"F0.wireOp",EDGE,"E4.7.3.0"),sQuery(id+"F0.wireOp",EDGE,"E4.7.4.0"),sQuery(id+"F0.wireOp",EDGE,"E4.7.5.0"),sQuery(id+"F0.wireOp",EDGE,"E4.7.6.0"),sQuery(id+"F0.wireOp",EDGE,"E4.7.7.0"),sQuery(id+"F0.wireOp",EDGE,"E4.7.8.0"),sQuery(id+"F0.wireOp",EDGE,"E4.7.9.0"),sQuery(id+"F0.wireOp",EDGE,"E4.7.10.0"),sQuery(id+"F0.wireOp",EDGE,"E4.8.0.0"),sQuery(id+"F0.wireOp",EDGE,"E4.8.1.0"),sQuery(id+"F0.wireOp",EDGE,"E4.8.2.0"),sQuery(id+"F0.wireOp",EDGE,"E4.8.3.0"),sQuery(id+"F0.wireOp",EDGE,"E4.8.4.0"),sQuery(id+"F0.wireOp",EDGE,"E4.8.5.0"),sQuery(id+"F0.wireOp",EDGE,"E4.8.6.0"),sQuery(id+"F0.wireOp",EDGE,"E4.8.7.0"),sQuery(id+"F0.wireOp",EDGE,"E4.8.8.0"),sQuery(id+"F0.wireOp",EDGE,"E4.8.9.0"),sQuery(id+"F0.wireOp",EDGE,"E4.8.10.0"),sQuery(id+"F0.wireOp",EDGE,"E4.9.0.0"),sQuery(id+"F0.wireOp",EDGE,"E4.9.1.0"),sQuery(id+"F0.wireOp",EDGE,"E4.9.2.0"),sQuery(id+"F0.wireOp",EDGE,"E4.9.3.0"),sQuery(id+"F0.wireOp",EDGE,"E4.9.4.0"),sQuery(id+"F0.wireOp",EDGE,"E4.9.5.0"),sQuery(id+"F0.wireOp",EDGE,"E4.9.6.0"),sQuery(id+"F0.wireOp",EDGE,"E4.9.7.0"),sQuery(id+"F0.wireOp",EDGE,"E4.9.8.0"),sQuery(id+"F0.wireOp",EDGE,"E4.9.9.0"),sQuery(id+"F0.wireOp",EDGE,"E4.9.10.0"),sQuery(id+"F0.wireOp",EDGE,"E4.10.0.0"),sQuery(id+"F0.wireOp",EDGE,"E4.10.1.0"),sQuery(id+"F0.wireOp",EDGE,"E4.10.2.0"),sQuery(id+"F0.wireOp",EDGE,"E4.10.3.0"),sQuery(id+"F0.wireOp",EDGE,"E4.10.4.0"),sQuery(id+"F0.wireOp",EDGE,"E4.10.5.0"),sQuery(id+"F0.wireOp",EDGE,"E4.10.6.0"),sQuery(id+"F0.wireOp",EDGE,"E4.10.7.0"),sQuery(id+"F0.wireOp",EDGE,"E4.10.8.0"),sQuery(id+"F0.wireOp",EDGE,"E4.10.9.0"),sQuery(id+"F0.wireOp",EDGE,"E4.10.10.0"),sQuery(id+"F0.wireOp",EDGE,"E4.11.0.0"),sQuery(id+"F0.wireOp",EDGE,"E4.11.1.0"),sQuery(id+"F0.wireOp",EDGE,"E4.11.2.0"),sQuery(id+"F0.wireOp",EDGE,"E4.11.3.0"),sQuery(id+"F0.wireOp",EDGE,"E4.11.4.0"),sQuery(id+"F0.wireOp",EDGE,"E4.11.5.0"),sQuery(id+"F0.wireOp",EDGE,"E4.11.6.0"),sQuery(id+"F0.wireOp",EDGE,"E4.11.7.0"),sQuery(id+"F0.wireOp",EDGE,"E4.11.8.0"),sQuery(id+"F0.wireOp",EDGE,"E4.11.9.0"),sQuery(id+"F0.wireOp",EDGE,"E4.11.10.0"),sQuery(id+"F0.wireOp",EDGE,"E4.12.0.0"),sQuery(id+"F0.wireOp",EDGE,"E4.12.1.0"),sQuery(id+"F0.wireOp",EDGE,"E4.12.2.0"),sQuery(id+"F0.wireOp",EDGE,"E4.12.3.0"),sQuery(id+"F0.wireOp",EDGE,"E4.12.4.0"),sQuery(id+"F0.wireOp",EDGE,"E4.12.5.0"),sQuery(id+"F0.wireOp",EDGE,"E4.12.6.0"),sQuery(id+"F0.wireOp",EDGE,"E4.12.7.0"),sQuery(id+"F0.wireOp",EDGE,"E4.12.8.0"),sQuery(id+"F0.wireOp",EDGE,"E4.12.9.0"),sQuery(id+"F0.wireOp",EDGE,"E4.12.10.0"),sQuery(id+"F0.wireOp",EDGE,"E4.13.0.0"),sQuery(id+"F0.wireOp",EDGE,"E4.13.1.0"),sQuery(id+"F0.wireOp",EDGE,"E4.13.2.0"),sQuery(id+"F0.wireOp",EDGE,"E4.13.3.0"),sQuery(id+"F0.wireOp",EDGE,"E4.13.4.0"),sQuery(id+"F0.wireOp",EDGE,"E4.13.5.0"),sQuery(id+"F0.wireOp",EDGE,"E4.13.6.0"),sQuery(id+"F0.wireOp",EDGE,"E4.13.7.0"),sQuery(id+"F0.wireOp",EDGE,"E4.13.8.0"),sQuery(id+"F0.wireOp",EDGE,"E4.13.9.0"),sQuery(id+"F0.wireOp",EDGE,"E4.13.10.0"),sQuery(id+"F0.wireOp",EDGE,"E4.14.0.0"),sQuery(id+"F0.wireOp",EDGE,"E4.14.1.0"),sQuery(id+"F0.wireOp",EDGE,"E4.14.2.0"),sQuery(id+"F0.wireOp",EDGE,"E4.14.3.0"),sQuery(id+"F0.wireOp",EDGE,"E4.14.4.0"),sQuery(id+"F0.wireOp",EDGE,"E4.14.5.0"),sQuery(id+"F0.wireOp",EDGE,"E4.14.6.0"),sQuery(id+"F0.wireOp",EDGE,"E4.14.7.0"),sQuery(id+"F0.wireOp",EDGE,"E4.14.8.0"),sQuery(id+"F0.wireOp",EDGE,"E4.14.9.0"),sQuery(id+"F0.wireOp",EDGE,"E4.14.10.0"),sQuery(id+"F0.wireOp",EDGE,"E4.15.0.0"),sQuery(id+"F0.wireOp",EDGE,"E4.15.1.0"),sQuery(id+"F0.wireOp",EDGE,"E4.15.2.0"),sQuery(id+"F0.wireOp",EDGE,"E4.15.3.0"),sQuery(id+"F0.wireOp",EDGE,"E4.15.4.0"),sQuery(id+"F0.wireOp",EDGE,"E4.15.5.0"),sQuery(id+"F0.wireOp",EDGE,"E4.15.6.0"),sQuery(id+"F0.wireOp",EDGE,"E4.15.7.0"),sQuery(id+"F0.wireOp",EDGE,"E4.15.8.0"),sQuery(id+"F0.wireOp",EDGE,"E4.15.9.0"),sQuery(id+"F0.wireOp",EDGE,"E4.15.10.0"),sQuery(id+"F0.wireOp",EDGE,"E4.16.0.0"),sQuery(id+"F0.wireOp",EDGE,"E4.16.1.0"),sQuery(id+"F0.wireOp",EDGE,"E4.16.2.0"),sQuery(id+"F0.wireOp",EDGE,"E4.16.3.0"),sQuery(id+"F0.wireOp",EDGE,"E4.16.4.0"),sQuery(id+"F0.wireOp",EDGE,"E4.16.5.0"),sQuery(id+"F0.wireOp",EDGE,"E4.16.6.0"),sQuery(id+"F0.wireOp",EDGE,"E4.16.7.0"),sQuery(id+"F0.wireOp",EDGE,"E4.16.8.0"),sQuery(id+"F0.wireOp",EDGE,"E4.16.9.0"),sQuery(id+"F0.wireOp",EDGE,"E4.16.10.0")])],"isStart":false});
            var sketch = newSketch(context, id + "F2", { "sketchPlane" : qUnion([Q0])});
            skLineSegment(sketch, "E5.bottom", {"start": v(-154.94, -101.6) * mm, "end": v(155.06, -101.6) * mm, "construction": true});
            skLineSegment(sketch, "E5.top", {"start": v(-154.94, 28.4) * mm, "end": v(155.06, 28.4) * mm, "construction": true});
            skLineSegment(sketch, "E5.left", {"start": v(-154.94, -101.6) * mm, "end": v(-154.94, 28.4) * mm, "construction": true});
            skLineSegment(sketch, "E5.right", {"start": v(155.06, -101.6) * mm, "end": v(155.06, 28.4) * mm, "construction": true});
            skLineSegment(sketch, "E6", {"start": v(-154.94, -101.6) * mm, "end": v(-154.94, -63.5) * mm});
            skLineSegment(sketch, "E7", {"start": v(-154.94, -101.6) * mm, "end": v(-116.84, -101.6) * mm});
            skLineSegment(sketch, "E8", {"start": v(-161.3, -63.5) * mm, "end": v(-161.3, -107.95) * mm});
            skLineSegment(sketch, "E9", {"start": v(-161.3, -107.95) * mm, "end": v(-116.84, -107.95) * mm});
            skLineSegment(sketch, "E10", {"start": v(-116.84, -101.6) * mm, "end": v(-116.84, -107.95) * mm});
            skLineSegment(sketch, "E11", {"start": v(-161.3, -63.5) * mm, "end": v(-154.94, -63.5) * mm});
            skLineSegment(sketch, "E12", {"start": v(-154.94, -36.6) * mm, "end": v(176.78, -36.6) * mm, "construction": true});
            skPoint(sketch, "E12.endSnap0", {"position": v(155.06, -36.6) * mm});
            skLineSegment(sketch, "E13", {"start": v(0.06, 28.4) * mm, "end": v(0.06, -178.16) * mm, "construction": true});
            skLineSegment(sketch, "E14.MirrorCS", {"start": v(-161.3, -9.7) * mm, "end": v(-154.94, -9.7) * mm});
            skLineSegment(sketch, "E15.MirrorCS", {"start": v(-161.3, -9.7) * mm, "end": v(-161.3, 34.75) * mm});
            skLineSegment(sketch, "E16.MirrorCS", {"start": v(-161.3, 34.75) * mm, "end": v(-116.84, 34.75) * mm});
            skLineSegment(sketch, "E17.MirrorCS", {"start": v(-116.84, 28.4) * mm, "end": v(-116.84, 34.75) * mm});
            skLineSegment(sketch, "E18.MirrorCS", {"start": v(161.4, 34.75) * mm, "end": v(116.96, 34.75) * mm});
            skLineSegment(sketch, "E19.MirrorCS", {"start": v(116.96, 28.4) * mm, "end": v(116.96, 34.75) * mm});
            skLineSegment(sketch, "E20.MirrorCS", {"start": v(161.4, -9.7) * mm, "end": v(161.4, 34.75) * mm});
            skLineSegment(sketch, "E21.MirrorCS", {"start": v(161.4, -9.7) * mm, "end": v(155.06, -9.7) * mm});
            skLineSegment(sketch, "E22.MirrorCS", {"start": v(161.4, -63.5) * mm, "end": v(161.4, -107.95) * mm});
            skLineSegment(sketch, "E23.MirrorCS", {"start": v(161.4, -63.5) * mm, "end": v(155.06, -63.5) * mm});
            skLineSegment(sketch, "E24.MirrorCS", {"start": v(161.4, -107.95) * mm, "end": v(116.96, -107.95) * mm});
            skLineSegment(sketch, "E25.MirrorCS", {"start": v(116.96, -101.6) * mm, "end": v(116.96, -107.95) * mm});
            skLineSegment(sketch, "E26", {"start": v(-154.94, -9.7) * mm, "end": v(-154.94, 28.4) * mm});
            skLineSegment(sketch, "E27", {"start": v(-116.84, 28.4) * mm, "end": v(-154.94, 28.4) * mm});
            skLineSegment(sketch, "E28", {"start": v(116.96, 28.4) * mm, "end": v(155.06, 28.4) * mm});
            skLineSegment(sketch, "E29", {"start": v(155.06, -9.7) * mm, "end": v(155.06, 28.4) * mm});
            skLineSegment(sketch, "E30", {"start": v(155.06, -63.5) * mm, "end": v(155.06, -101.6) * mm});
            skLineSegment(sketch, "E31", {"start": v(116.96, -101.6) * mm, "end": v(155.06, -101.6) * mm});
            skSolve(sketch);
        }
        {
            var Q0;
            {var subQ11=sQuery(id+"F2.wireOp",EDGE,"E14.MirrorCS");Q0=makeQuery(id+"F2.imprint","IMPRINT",FACE,{"disambiguationData":[TD([[makeQuery(id+"F2.imprint","IMPRINT",EDGE,{"derivedFrom":subQ11}),1.0]])]});}
            var Q1;
            Q1=makeQuery(id+"F2.imprint","IMPRINT",FACE,{"disambiguationData":[TD([[makeQuery(id+"F2.imprint","IMPRINT",EDGE,{"derivedFrom":sQuery(id+"F2.wireOp",EDGE,"E8")}),1.0]])]});
            var Q2;
            Q2=makeQuery(id+"F2.imprint","IMPRINT",FACE,{"disambiguationData":[TD([[makeQuery(id+"F2.imprint","IMPRINT",EDGE,{"derivedFrom":sQuery(id+"F2.wireOp",EDGE,"E18.MirrorCS")}),1.0]])]});
            var Q3;
            Q3=makeQuery(id+"F2.imprint","IMPRINT",FACE,{"disambiguationData":[TD([[makeQuery(id+"F2.imprint","IMPRINT",EDGE,{"derivedFrom":sQuery(id+"F2.wireOp",EDGE,"E22.MirrorCS")}),-1.0]])]});
            extrude(context, id + "F3", {"entities" : qUnion([Q0, Q1, Q2, Q3]), "depth" : 27 * mm});
        }
        {
            var Q0;
            {var subQ0=sQuery(id+"F0.wireOp",EDGE,"E4.16.10.0");var subQ1=sQuery(id+"F0.wireOp",EDGE,"E4.14.9.0");var subQ2=sQuery(id+"F0.wireOp",EDGE,"E4.16.8.0");var subQ3=sQuery(id+"F0.wireOp",EDGE,"E4.16.7.0");var subQ4=sQuery(id+"F0.wireOp",EDGE,"E4.12.9.0");var subQ5=sQuery(id+"F0.wireOp",EDGE,"E4.2.2.0");var subQ6=sQuery(id+"F0.wireOp",EDGE,"E4.16.6.0");var subQ7=sQuery(id+"F0.wireOp",EDGE,"E4.12.8.0");var subQ8=sQuery(id+"F0.wireOp",EDGE,"E4.16.5.0");var subQ9=sQuery(id+"F0.wireOp",EDGE,"E4.1.3.0");var subQ10=sQuery(id+"F0.wireOp",EDGE,"E4.16.4.0");var subQ11=sQuery(id+"F0.wireOp",EDGE,"E4.15.9.0");var subQ12=sQuery(id+"F0.wireOp",EDGE,"E4.15.8.0");var subQ13=sQuery(id+"F0.wireOp",EDGE,"E4.0.6.0");var subQ14=sQuery(id+"F0.wireOp",EDGE,"E4.15.7.0");var subQ15=sQuery(id+"F0.wireOp",EDGE,"E4.15.6.0");var subQ16=sQuery(id+"F0.wireOp",EDGE,"E4.4.10.0");var subQ17=sQuery(id+"F0.wireOp",EDGE,"E4.15.5.0");var subQ18=sQuery(id+"F0.wireOp",EDGE,"E4.11.7.0");var subQ21=sQuery(id+"F0.wireOp",EDGE,"E4.3.4.0");var subQ23=sQuery(id+"F0.wireOp",EDGE,"E4.2.4.0");var subQ26=sQuery(id+"F0.wireOp",EDGE,"E4.15.3.0");var subQ27=sQuery(id+"F0.wireOp",EDGE,"E4.0.9.0");var subQ28=sQuery(id+"F0.wireOp",EDGE,"E4.15.1.0");var subQ29=sQuery(id+"F0.wireOp",EDGE,"E4.11.3.0");var subQ30=sQuery(id+"F0.wireOp",EDGE,"E4.15.0.0");var subQ31=sQuery(id+"F0.wireOp",EDGE,"E4.8.2.0");var subQ32=sQuery(id+"F0.wireOp",EDGE,"E4.14.8.0");var subQ33=sQuery(id+"F0.wireOp",EDGE,"E4.14.5.0");var subQ36=sQuery(id+"F0.wireOp",EDGE,"E4.2.5.0");var subQ38=sQuery(id+"F0.wireOp",EDGE,"E4.13.4.0");var subQ39=sQuery(id+"F0.wireOp",EDGE,"E4.14.4.0");var subQ41=sQuery(id+"F0.wireOp",EDGE,"E4.13.9.0");var subQ42=sQuery(id+"F0.wireOp",EDGE,"E4.14.3.0");var subQ43=sQuery(id+"F0.wireOp",EDGE,"E4.16.9.0");var subQ44=sQuery(id+"F0.wireOp",EDGE,"E4.1.7.0");var subQ45=sQuery(id+"F0.wireOp",EDGE,"E4.14.2.0");var subQ46=sQuery(id+"F0.wireOp",EDGE,"E4.3.6.0");var subQ47=sQuery(id+"F0.wireOp",EDGE,"E4.15.4.0");var subQ48=sQuery(id+"F0.wireOp",EDGE,"E4.8.6.0");var subQ49=sQuery(id+"F0.wireOp",EDGE,"E4.14.0.0");var subQ51=sQuery(id+"F0.wireOp",EDGE,"E4.2.9.0");var subQ52=sQuery(id+"F0.wireOp",EDGE,"E4.13.10.0");var subQ53=sQuery(id+"F0.wireOp",EDGE,"E4.13.1.0");var subQ54=sQuery(id+"F0.wireOp",EDGE,"E4.13.0.0");var subQ55=sQuery(id+"F0.wireOp",EDGE,"E4.12.10.0");var subQ58=sQuery(id+"F0.wireOp",EDGE,"E4.3.9.0");var subQ60=sQuery(id+"F0.wireOp",EDGE,"E4.12.7.0");var subQ61=sQuery(id+"F0.wireOp",EDGE,"E4.15.2.0");var subQ62=sQuery(id+"F0.wireOp",EDGE,"E4.11.4.0");var subQ63=sQuery(id+"F0.wireOp",EDGE,"E4.12.6.0");var subQ64=sQuery(id+"F0.wireOp",EDGE,"E4.8.8.0");var subQ66=sQuery(id+"F0.wireOp",EDGE,"E4.2.8.0");var subQ68=sQuery(id+"F0.wireOp",EDGE,"E4.12.3.0");var subQ69=sQuery(id+"F0.wireOp",EDGE,"E4.8.5.0");var subQ70=sQuery(id+"F0.wireOp",EDGE,"E4.13.7.0");var subQ71=sQuery(id+"F0.wireOp",EDGE,"E4.9.9.0");var subQ72=sQuery(id+"F0.wireOp",EDGE,"E4.11.8.0");var subQ74=sQuery(id+"F0.wireOp",EDGE,"E4.16.2.0");var subQ75=sQuery(id+"F0.wireOp",EDGE,"E4.12.4.0");var subQ76=sQuery(id+"F0.wireOp",EDGE,"E4.11.6.0");var subQ78=sQuery(id+"F0.wireOp",EDGE,"E4.14.1.0");var subQ79=sQuery(id+"F0.wireOp",EDGE,"E4.10.3.0");var subQ80=sQuery(id+"F0.wireOp",EDGE,"E4.11.5.0");var subQ81=sQuery(id+"F0.wireOp",EDGE,"E4.11.2.0");var subQ82=sQuery(id+"F0.wireOp",EDGE,"E4.7.4.0");var subQ83=sQuery(id+"F0.wireOp",EDGE,"E4.13.8.0");var subQ84=sQuery(id+"F0.wireOp",EDGE,"E4.9.10.0");var subQ85=sQuery(id+"F0.wireOp",EDGE,"E4.11.1.0");var subQ86=sQuery(id+"F0.wireOp",EDGE,"E4.10.10.0");var subQ87=sQuery(id+"F0.wireOp",EDGE,"E4.16.3.0");var subQ88=sQuery(id+"F0.wireOp",EDGE,"E4.1.9.0");var subQ89=sQuery(id+"F0.wireOp",EDGE,"E4.10.4.0");var subQ90=sQuery(id+"F0.wireOp",EDGE,"E4.11.0.0");var subQ91=sQuery(id+"F0.wireOp",EDGE,"E4.12.2.0");var subQ92=sQuery(id+"F0.wireOp",EDGE,"E4.8.4.0");var subQ93=sQuery(id+"F0.wireOp",EDGE,"E4.10.2.0");var subQ94=sQuery(id+"F0.wireOp",EDGE,"E4.10.1.0");var subQ97=sQuery(id+"F0.wireOp",EDGE,"E4.15.10.0");var subQ98=sQuery(id+"F0.wireOp",EDGE,"E4.1.5.0");var subQ99=sQuery(id+"F0.wireOp",EDGE,"E4.10.0.0");var subQ100=sQuery(id+"F0.wireOp",EDGE,"E4.6.2.0");var subQ101=sQuery(id+"F0.wireOp",EDGE,"E4.11.9.0");var subQ102=sQuery(id+"F0.wireOp",EDGE,"E4.12.5.0");var subQ103=sQuery(id+"F0.wireOp",EDGE,"E4.9.8.0");var subQ104=sQuery(id+"F0.wireOp",EDGE,"E4.9.7.0");var subQ105=sQuery(id+"F0.wireOp",EDGE,"E4.5.9.0");var subQ106=sQuery(id+"F0.wireOp",EDGE,"E4.9.3.0");var subQ107=sQuery(id+"F0.wireOp",EDGE,"E4.5.5.0");var subQ108=sQuery(id+"F0.wireOp",EDGE,"E4.14.10.0");var subQ109=sQuery(id+"F0.wireOp",EDGE,"E4.0.5.0");var subQ110=sQuery(id+"F0.wireOp",EDGE,"E4.9.0.0");var subQ111=sQuery(id+"F0.wireOp",EDGE,"E4.8.10.0");var subQ112=sQuery(id+"F0.wireOp",EDGE,"E4.8.9.0");var subQ116=sQuery(id+"F0.wireOp",EDGE,"E4.13.3.0");var subQ117=sQuery(id+"F0.wireOp",EDGE,"E4.9.5.0");var subQ118=sQuery(id+"F0.wireOp",EDGE,"E4.12.1.0");var subQ119=sQuery(id+"F0.wireOp",EDGE,"E3");var subQ120=sQuery(id+"F0.wireOp",EDGE,"E4.3.1.0");var subQ121=sQuery(id+"F0.wireOp",EDGE,"E4.11.10.0");var subQ122=sQuery(id+"F0.wireOp",EDGE,"E4.8.1.0");var subQ123=sQuery(id+"F0.wireOp",EDGE,"E4.3.7.0");var subQ124=sQuery(id+"F0.wireOp",EDGE,"E4.9.6.0");var subQ125=sQuery(id+"F0.wireOp",EDGE,"E4.4.7.0");var subQ126=sQuery(id+"F0.wireOp",EDGE,"E4.7.0.0");var subQ127=sQuery(id+"F0.wireOp",EDGE,"E4.10.9.0");var subQ128=sQuery(id+"F0.wireOp",EDGE,"E4.9.2.0");var subQ129=sQuery(id+"F0.wireOp",EDGE,"E4.3.8.0");var subQ130=sQuery(id+"F0.wireOp",EDGE,"E4.3.0.0");var subQ131=sQuery(id+"F0.wireOp",EDGE,"E4.10.7.0");var subQ132=sQuery(id+"F0.wireOp",EDGE,"E4.2.1.0");var subQ135=sQuery(id+"F0.wireOp",EDGE,"E4.6.9.0");var subQ136=sQuery(id+"F0.wireOp",EDGE,"E4.10.6.0");var subQ137=sQuery(id+"F0.wireOp",EDGE,"E4.2.0.0");var subQ138=sQuery(id+"F0.wireOp",EDGE,"E4.7.8.0");var subQ139=sQuery(id+"F0.wireOp",EDGE,"E4.2.7.0");var subQ140=sQuery(id+"F0.wireOp",EDGE,"E4.6.5.0");var subQ141=sQuery(id+"F0.wireOp",EDGE,"E4.1.8.0");var subQ142=sQuery(id+"F0.wireOp",EDGE,"E4.2.6.0");var subQ143=sQuery(id+"F0.wireOp",EDGE,"E4.6.4.0");var subQ144=sQuery(id+"F0.wireOp",EDGE,"E4.5.2.0");var subQ145=sQuery(id+"F0.wireOp",EDGE,"E4.0.3.0");var subQ146=sQuery(id+"F0.wireOp",EDGE,"E4.5.0.0");var subQ147=sQuery(id+"F0.wireOp",EDGE,"E4.1.2.0");var subQ148=sQuery(id+"F0.wireOp",EDGE,"E4.0.10.0");var subQ149=sQuery(id+"F0.wireOp",EDGE,"E4.16.1.0");var subQ150=sQuery(id+"F0.wireOp",EDGE,"E4.7.6.0");var subQ151=sQuery(id+"F0.wireOp",EDGE,"E4.0.2.0");var subQ152=sQuery(id+"F0.wireOp",EDGE,"E4.0.1.0");var subQ153=sQuery(id+"F0.wireOp",EDGE,"E4.14.6.0");var subQ154=sQuery(id+"F0.wireOp",EDGE,"E4.8.7.0");var subQ155=sQuery(id+"F0.wireOp",EDGE,"E4.4.9.0");var subQ156=sQuery(id+"F0.wireOp",EDGE,"E4.6.0.0");var subQ157=sQuery(id+"F0.wireOp",EDGE,"E0.bottom");var subQ158=sQuery(id+"F0.wireOp",EDGE,"E4.1.1.0");var subQ159=sQuery(id+"F0.wireOp",EDGE,"E4.0.4.0");var subQ160=sQuery(id+"F0.wireOp",EDGE,"E4.4.2.0");var subQ161=sQuery(id+"F0.wireOp",EDGE,"E0.top");var subQ162=sQuery(id+"F0.wireOp",EDGE,"E4.8.3.0");var subQ163=sQuery(id+"F0.wireOp",EDGE,"E4.4.5.0");var subQ164=sQuery(id+"F0.wireOp",EDGE,"E4.5.7.0");var subQ165=sQuery(id+"F0.wireOp",EDGE,"E0.left");var subQ166=sQuery(id+"F0.wireOp",EDGE,"E4.12.0.0");var subQ167=sQuery(id+"F0.wireOp",EDGE,"E4.3.5.0");var subQ169=sQuery(id+"F0.wireOp",EDGE,"E0.right");var subQ170=sQuery(id+"F0.wireOp",EDGE,"E4.0.7.0");var subQ171=sQuery(id+"F0.wireOp",EDGE,"E4.1.0.0");var subQ172=sQuery(id+"F0.wireOp",EDGE,"E4.13.5.0");var subQ173=sQuery(id+"F0.wireOp",EDGE,"E4.9.1.0");var subQ174=sQuery(id+"F0.wireOp",EDGE,"E4.3.2.0");var subQ175=sQuery(id+"F0.wireOp",EDGE,"E4.7.10.0");var subQ176=sQuery(id+"F0.wireOp",EDGE,"E4.4.1.0");var subQ177=sQuery(id+"F0.wireOp",EDGE,"E4.5.3.0");var subQ178=sQuery(id+"F0.wireOp",EDGE,"E4.5.4.0");var subQ179=sQuery(id+"F0.wireOp",EDGE,"E4.1.6.0");var subQ180=sQuery(id+"F0.wireOp",EDGE,"E4.8.0.0");var subQ181=sQuery(id+"F0.wireOp",EDGE,"E4.2.3.0");var subQ182=sQuery(id+"F0.wireOp",EDGE,"E4.1.4.0");var subQ183=sQuery(id+"F0.wireOp",EDGE,"E4.2.10.0");var subQ184=sQuery(id+"F0.wireOp",EDGE,"E4.6.8.0");var subQ185=sQuery(id+"F0.wireOp",EDGE,"E4.5.6.0");var subQ186=sQuery(id+"F0.wireOp",EDGE,"E4.9.4.0");var subQ187=sQuery(id+"F0.wireOp",EDGE,"E4.0.8.0");var subQ188=sQuery(id+"F0.wireOp",EDGE,"E4.4.6.0");var subQ189=sQuery(id+"F0.wireOp",EDGE,"E4.6.6.0");var subQ190=sQuery(id+"F0.wireOp",EDGE,"E4.3.10.0");var subQ191=sQuery(id+"F0.wireOp",EDGE,"E4.6.7.0");var subQ192=sQuery(id+"F0.wireOp",EDGE,"E4.4.0.0");var subQ193=sQuery(id+"F0.wireOp",EDGE,"E4.7.9.0");var subQ194=sQuery(id+"F0.wireOp",EDGE,"E4.6.10.0");var subQ195=sQuery(id+"F0.wireOp",EDGE,"E4.10.8.0");var subQ196=sQuery(id+"F0.wireOp",EDGE,"E4.4.3.0");var subQ197=sQuery(id+"F0.wireOp",EDGE,"E4.4.4.0");var subQ198=sQuery(id+"F0.wireOp",EDGE,"E4.1.10.0");var subQ199=sQuery(id+"F0.wireOp",EDGE,"E4.5.8.0");var subQ200=sQuery(id+"F0.wireOp",EDGE,"E4.10.5.0");var subQ201=sQuery(id+"F0.wireOp",EDGE,"E4.4.8.0");var subQ202=sQuery(id+"F0.wireOp",EDGE,"E4.5.1.0");var subQ203=sQuery(id+"F0.wireOp",EDGE,"E4.3.3.0");var subQ204=sQuery(id+"F0.wireOp",EDGE,"E4.7.1.0");var subQ205=sQuery(id+"F0.wireOp",EDGE,"E4.5.10.0");var subQ206=sQuery(id+"F0.wireOp",EDGE,"E4.14.7.0");var subQ207=sQuery(id+"F0.wireOp",EDGE,"E4.6.1.0");var subQ208=sQuery(id+"F0.wireOp",EDGE,"E4.6.3.0");var subQ209=sQuery(id+"F0.wireOp",EDGE,"E4.7.2.0");var subQ210=sQuery(id+"F0.wireOp",EDGE,"E4.13.2.0");var subQ211=sQuery(id+"F0.wireOp",EDGE,"E4.7.3.0");var subQ212=sQuery(id+"F0.wireOp",EDGE,"E4.16.0.0");var subQ213=sQuery(id+"F0.wireOp",EDGE,"E4.7.5.0");var subQ214=sQuery(id+"F0.wireOp",EDGE,"E4.13.6.0");var subQ215=sQuery(id+"F0.wireOp",EDGE,"E4.7.7.0");Q0=makeQuery(id+"F3.boolean.opBoolean","SPLIT",FACE,{"disambiguationData":[TD([makeQuery(id+"F1.opExtrude","SWEPT_FACE",FACE,{"disambiguationData":[OSD([subQ157])]})])],"derivedFrom":makeQuery(id+"F1.opExtrude","CAP_FACE",FACE,{"disambiguationData":[OSD([subQ157,subQ161,subQ165,subQ169,subQ119,subQ152,subQ151,subQ145,subQ159,subQ109,subQ13,subQ170,subQ187,subQ27,subQ148,subQ171,subQ158,subQ147,subQ9,subQ182,subQ98,subQ179,subQ44,subQ141,subQ88,subQ198,subQ137,subQ132,subQ5,subQ181,subQ23,subQ36,subQ142,subQ139,subQ66,subQ51,subQ183,subQ130,subQ120,subQ174,subQ203,subQ21,subQ167,subQ46,subQ123,subQ129,subQ58,subQ190,subQ192,subQ176,subQ160,subQ196,subQ197,subQ163,subQ188,subQ125,subQ201,subQ155,subQ16,subQ146,subQ202,subQ144,subQ177,subQ178,subQ107,subQ185,subQ164,subQ199,subQ105,subQ205,subQ156,subQ207,subQ100,subQ208,subQ143,subQ140,subQ189,subQ191,subQ184,subQ135,subQ194,subQ126,subQ204,subQ209,subQ211,subQ82,subQ213,subQ150,subQ215,subQ138,subQ193,subQ175,subQ180,subQ122,subQ31,subQ162,subQ92,subQ69,subQ48,subQ154,subQ64,subQ112,subQ111,subQ110,subQ173,subQ128,subQ106,subQ186,subQ117,subQ124,subQ104,subQ103,subQ71,subQ84,subQ99,subQ94,subQ93,subQ79,subQ89,subQ200,subQ136,subQ131,subQ195,subQ127,subQ86,subQ90,subQ85,subQ81,subQ29,subQ62,subQ80,subQ76,subQ18,subQ72,subQ101,subQ121,subQ166,subQ118,subQ91,subQ68,subQ75,subQ102,subQ63,subQ60,subQ7,subQ4,subQ55,subQ54,subQ53,subQ210,subQ116,subQ38,subQ172,subQ214,subQ70,subQ83,subQ41,subQ52,subQ49,subQ78,subQ45,subQ42,subQ39,subQ33,subQ153,subQ206,subQ32,subQ1,subQ108,subQ30,subQ28,subQ61,subQ26,subQ47,subQ17,subQ15,subQ14,subQ12,subQ11,subQ97,subQ212,subQ149,subQ74,subQ87,subQ10,subQ8,subQ6,subQ3,subQ2,subQ43,subQ0])],"isStart":false})});}
            var sketch = newSketch(context, id + "F4", { "sketchPlane" : qUnion([Q0])});
            skLineSegment(sketch, "E32.bottom", {"start": v(-154.94, 28.4) * mm, "end": v(-116.84, 28.4) * mm});
            skLineSegment(sketch, "E32.top", {"start": v(-154.94, -9.7) * mm, "end": v(-116.84, -9.7) * mm});
            skLineSegment(sketch, "E32.left", {"start": v(-154.94, 28.4) * mm, "end": v(-154.94, -9.7) * mm});
            skLineSegment(sketch, "E32.right", {"start": v(-116.84, 28.4) * mm, "end": v(-116.84, -9.7) * mm});
            skLineSegment(sketch, "E33.bottom", {"start": v(-161.3, 34.75) * mm, "end": v(161.4, 34.75) * mm, "construction": true});
            skLineSegment(sketch, "E33.top", {"start": v(-161.3, -107.95) * mm, "end": v(161.4, -107.95) * mm, "construction": true});
            skLineSegment(sketch, "E33.left", {"start": v(-161.3, 34.75) * mm, "end": v(-161.3, -107.95) * mm, "construction": true});
            skLineSegment(sketch, "E33.right", {"start": v(161.41, 34.75) * mm, "end": v(161.41, -107.95) * mm, "construction": true});
            skLineSegment(sketch, "E34", {"start": v(-161.3, -36.6) * mm, "end": v(161.4, -36.6) * mm, "construction": true});
            skLineSegment(sketch, "E35", {"start": v(0.06, 34.75) * mm, "end": v(0.06, -107.95) * mm, "construction": true});
            skLineSegment(sketch, "E36.MirrorCS", {"start": v(155.06, 28.4) * mm, "end": v(116.96, 28.4) * mm});
            skLineSegment(sketch, "E37.MirrorCS", {"start": v(155.06, 28.4) * mm, "end": v(155.06, -9.7) * mm});
            skLineSegment(sketch, "E38.MirrorCS", {"start": v(155.06, -9.7) * mm, "end": v(116.96, -9.7) * mm});
            skLineSegment(sketch, "E39.MirrorCS", {"start": v(116.96, 28.4) * mm, "end": v(116.96, -9.7) * mm});
            skLineSegment(sketch, "E40.MirrorCS", {"start": v(-154.94, -101.6) * mm, "end": v(-116.84, -101.6) * mm});
            skLineSegment(sketch, "E41.MirrorCS", {"start": v(-154.94, -101.6) * mm, "end": v(-154.94, -63.5) * mm});
            skLineSegment(sketch, "E42.MirrorCS", {"start": v(-154.94, -63.5) * mm, "end": v(-116.84, -63.5) * mm});
            skLineSegment(sketch, "E43.MirrorCS", {"start": v(-116.84, -101.6) * mm, "end": v(-116.84, -63.5) * mm});
            skLineSegment(sketch, "E44.MirrorCS", {"start": v(155.06, -101.6) * mm, "end": v(116.96, -101.6) * mm});
            skLineSegment(sketch, "E45.MirrorCS", {"start": v(116.96, -101.6) * mm, "end": v(116.96, -63.5) * mm});
            skLineSegment(sketch, "E46.MirrorCS", {"start": v(155.06, -63.5) * mm, "end": v(116.96, -63.5) * mm});
            skLineSegment(sketch, "E47.MirrorCS", {"start": v(155.06, -101.6) * mm, "end": v(155.06, -63.5) * mm});
            skLineSegment(sketch, "E48", {"start": v(-186.7, -9.7) * mm, "end": v(-186.7, 60.15) * mm});
            skLineSegment(sketch, "E49", {"start": v(-186.7, 60.15) * mm, "end": v(-116.84, 60.15) * mm});
            skLineSegment(sketch, "E50", {"start": v(-116.84, 60.15) * mm, "end": v(-116.84, 34.75) * mm});
            skLineSegment(sketch, "E51", {"start": v(-116.84, 34.75) * mm, "end": v(-161.3, 34.75) * mm});
            skLineSegment(sketch, "E52", {"start": v(-161.3, 34.75) * mm, "end": v(-161.3, -9.7) * mm});
            skLineSegment(sketch, "E53", {"start": v(-161.3, -9.7) * mm, "end": v(-186.7, -9.7) * mm});
            skPoint(sketch, "E54", {"position": v(-177.8, 25.4) * mm});
            skPoint(sketch, "E55", {"position": v(-152.4, 50.8) * mm});
            skLineSegment(sketch, "E56.MirrorCS", {"start": v(186.8, 60.15) * mm, "end": v(116.96, 60.15) * mm});
            skLineSegment(sketch, "E57.MirrorCS", {"start": v(116.96, 60.15) * mm, "end": v(116.96, 34.75) * mm});
            skLineSegment(sketch, "E58.MirrorCS", {"start": v(186.8, -9.7) * mm, "end": v(186.8, 60.15) * mm});
            skLineSegment(sketch, "E59.MirrorCS", {"start": v(161.4, -9.7) * mm, "end": v(186.8, -9.7) * mm});
            skLineSegment(sketch, "E60.MirrorCS", {"start": v(-186.7, -133.35) * mm, "end": v(-116.84, -133.35) * mm});
            skLineSegment(sketch, "E61.MirrorCS", {"start": v(-186.7, -63.5) * mm, "end": v(-186.7, -133.35) * mm});
            skLineSegment(sketch, "E62.MirrorCS", {"start": v(-161.3, -63.5) * mm, "end": v(-186.7, -63.5) * mm});
            skLineSegment(sketch, "E63.MirrorCS", {"start": v(-116.84, -133.35) * mm, "end": v(-116.84, -107.95) * mm});
            skLineSegment(sketch, "E64.MirrorCS", {"start": v(186.8, -133.35) * mm, "end": v(116.96, -133.35) * mm});
            skLineSegment(sketch, "E65.MirrorCS", {"start": v(116.96, -133.35) * mm, "end": v(116.96, -107.95) * mm});
            skLineSegment(sketch, "E66.MirrorCS", {"start": v(161.4, -63.5) * mm, "end": v(186.8, -63.5) * mm});
            skLineSegment(sketch, "E67.MirrorCS", {"start": v(186.8, -63.5) * mm, "end": v(186.8, -133.35) * mm});
            skLineSegment(sketch, "E68", {"start": v(-161.3, -63.5) * mm, "end": v(-161.3, -107.95) * mm});
            skLineSegment(sketch, "E69", {"start": v(-161.3, -107.95) * mm, "end": v(-116.84, -107.95) * mm});
            skLineSegment(sketch, "E70", {"start": v(116.96, 34.75) * mm, "end": v(161.4, 34.75) * mm});
            skLineSegment(sketch, "E71", {"start": v(161.4, 34.75) * mm, "end": v(161.4, -9.7) * mm});
            skLineSegment(sketch, "E72", {"start": v(161.4, -63.5) * mm, "end": v(161.4, -107.95) * mm});
            skLineSegment(sketch, "E73", {"start": v(161.41, -107.95) * mm, "end": v(116.96, -107.95) * mm});
            skPoint(sketch, "E74", {"position": v(-177.8, -101.6) * mm});
            skPoint(sketch, "E75", {"position": v(-152.4, -127) * mm});
            skPoint(sketch, "E76", {"position": v(152.4, -127) * mm});
            skPoint(sketch, "E77", {"position": v(177.8, -101.6) * mm});
            skPoint(sketch, "E78", {"position": v(152.4, 50.8) * mm});
            skPoint(sketch, "E79.middle", {"position": v(177.8, 25.4) * mm});
            skCircle(sketch, "E80", {"center": v(-152.4, 50.8) * mm, "radius": 3.97 * mm});
            skCircle(sketch, "E81", {"center": v(-177.8, 25.4) * mm, "radius": 3.97 * mm});
            skCircle(sketch, "E82", {"center": v(-177.8, -101.6) * mm, "radius": 3.97 * mm});
            skCircle(sketch, "E83", {"center": v(-152.4, -127) * mm, "radius": 3.97 * mm});
            skCircle(sketch, "E84", {"center": v(152.4, 50.8) * mm, "radius": 3.97 * mm});
            skCircle(sketch, "E85", {"center": v(177.8, 25.4) * mm, "radius": 3.97 * mm});
            skCircle(sketch, "E86", {"center": v(177.8, -101.6) * mm, "radius": 3.97 * mm});
            skCircle(sketch, "E87", {"center": v(152.4, -127) * mm, "radius": 3.97 * mm});
            skSolve(sketch);
        }
        {
            var Q0;
            {var subQ5=sQuery(id+"F4.wireOp",EDGE,"E32.top");Q0=makeQuery(id+"F4.imprint","IMPRINT",FACE,{"disambiguationData":[TD([[makeQuery(id+"F4.imprint","IMPRINT",EDGE,{"derivedFrom":subQ5}),1.0]])]});}
            var Q1;
            {var subQ0=sQuery(id+"F4.wireOp",EDGE,"E38.MirrorCS");Q1=makeQuery(id+"F4.imprint","IMPRINT",FACE,{"disambiguationData":[TD([[makeQuery(id+"F4.imprint","IMPRINT",EDGE,{"derivedFrom":subQ0}),-1.0]])]});}
            var Q2;
            {var subQ0=sQuery(id+"F4.wireOp",EDGE,"E42.MirrorCS");Q2=makeQuery(id+"F4.imprint","IMPRINT",FACE,{"disambiguationData":[TD([[makeQuery(id+"F4.imprint","IMPRINT",EDGE,{"derivedFrom":subQ0}),-1.0]])]});}
            var Q3;
            {var subQ1=sQuery(id+"F4.wireOp",EDGE,"E45.MirrorCS");Q3=makeQuery(id+"F4.imprint","IMPRINT",FACE,{"disambiguationData":[TD([[makeQuery(id+"F4.imprint","IMPRINT",EDGE,{"derivedFrom":subQ1}),-1.0]])]});}
            extrude(context, id + "F5", {"entities" : qUnion([Q0, Q1, Q2, Q3]), "operationType" : NewBodyOperationType.ADD, "depth" : 17 * mm});
        }
        {
            var Q0;
            Q0=makeQuery(id+"F4.imprint","IMPRINT",FACE,{"disambiguationData":[TD([[makeQuery(id+"F4.imprint","IMPRINT",EDGE,{"derivedFrom":sQuery(id+"F4.wireOp",EDGE,"E48")}),-1.0]])]});
            var Q1;
            Q1=makeQuery(id+"F4.imprint","IMPRINT",FACE,{"disambiguationData":[TD([[makeQuery(id+"F4.imprint","IMPRINT",EDGE,{"derivedFrom":sQuery(id+"F4.wireOp",EDGE,"E60.MirrorCS")}),1.0]])]});
            var Q2;
            Q2=makeQuery(id+"F4.imprint","IMPRINT",FACE,{"disambiguationData":[TD([[makeQuery(id+"F4.imprint","IMPRINT",EDGE,{"derivedFrom":sQuery(id+"F4.wireOp",EDGE,"E56.MirrorCS")}),1.0]])]});
            var Q3;
            Q3=makeQuery(id+"F4.imprint","IMPRINT",FACE,{"disambiguationData":[TD([[makeQuery(id+"F4.imprint","IMPRINT",EDGE,{"derivedFrom":sQuery(id+"F4.wireOp",EDGE,"E64.MirrorCS")}),-1.0]])]});
            extrude(context, id + "F6", {"entities" : qUnion([Q0, Q1, Q2, Q3]), "operationType" : NewBodyOperationType.ADD, "depth" : 5.08 * mm});
        }
        {
            var Q0;
            Q0=makeQuery(id+"F3.opExtrude","CAP_FACE",FACE,{"disambiguationData":[OSD([sQuery(id+"F2.wireOp",EDGE,"E6"),sQuery(id+"F2.wireOp",EDGE,"E7"),sQuery(id+"F2.wireOp",EDGE,"E8"),sQuery(id+"F2.wireOp",EDGE,"E9"),sQuery(id+"F2.wireOp",EDGE,"E10"),sQuery(id+"F2.wireOp",EDGE,"E11")])],"isStart":false});
            var sketch = newSketch(context, id + "F7", { "sketchPlane" : qUnion([Q0])});
            skLineSegment(sketch, "E88.bottom", {"start": v(-150.12, -101.6) * mm, "end": v(-143.77, -101.6) * mm});
            skLineSegment(sketch, "E88.top", {"start": v(-150.12, -104.14) * mm, "end": v(-143.77, -104.14) * mm});
            skLineSegment(sketch, "E88.left", {"start": v(-150.12, -101.6) * mm, "end": v(-150.12, -104.14) * mm});
            skLineSegment(sketch, "E88.right", {"start": v(-143.77, -101.6) * mm, "end": v(-143.77, -104.14) * mm});
            skLineSegment(sketch, "E89.bottom", {"start": v(-154.94, -85.73) * mm, "end": v(-157.99, -85.73) * mm});
            skLineSegment(sketch, "E89.top", {"start": v(-154.94, -79.38) * mm, "end": v(-157.99, -79.38) * mm});
            skLineSegment(sketch, "E89.left", {"start": v(-154.94, -85.73) * mm, "end": v(-154.94, -79.38) * mm});
            skLineSegment(sketch, "E89.right", {"start": v(-157.99, -85.73) * mm, "end": v(-157.99, -79.38) * mm});
            skLineSegment(sketch, "E90.MirrorCS", {"start": v(-154.94, 12.52) * mm, "end": v(-154.94, 6.17) * mm});
            skLineSegment(sketch, "E91.MirrorCS", {"start": v(-157.99, 12.52) * mm, "end": v(-157.99, 6.17) * mm});
            skLineSegment(sketch, "E92.MirrorCS", {"start": v(-154.94, 6.17) * mm, "end": v(-157.99, 6.17) * mm});
            skLineSegment(sketch, "E93.MirrorCS", {"start": v(-154.94, 12.52) * mm, "end": v(-157.99, 12.52) * mm});
            skLineSegment(sketch, "E94.MirrorCS", {"start": v(-150.12, 28.4) * mm, "end": v(-143.77, 28.4) * mm});
            skLineSegment(sketch, "E95.MirrorCS", {"start": v(-150.12, 28.4) * mm, "end": v(-150.12, 30.94) * mm});
            skLineSegment(sketch, "E96.MirrorCS", {"start": v(-150.12, 30.94) * mm, "end": v(-143.77, 30.94) * mm});
            skLineSegment(sketch, "E97.MirrorCS", {"start": v(-143.77, 28.4) * mm, "end": v(-143.77, 30.94) * mm});
            skSolve(sketch);
        }
        {
            var Q0;
            Q0=makeQuery(id+"F7.imprint","IMPRINT",FACE,{"disambiguationData":[TD([[makeQuery(id+"F7.imprint","IMPRINT",EDGE,{"derivedFrom":sQuery(id+"F7.wireOp",EDGE,"E94.MirrorCS")}),1.0]])]});
            var Q1;
            Q1=makeQuery(id+"F7.imprint","IMPRINT",FACE,{"disambiguationData":[TD([[makeQuery(id+"F7.imprint","IMPRINT",EDGE,{"derivedFrom":sQuery(id+"F7.wireOp",EDGE,"E90.MirrorCS")}),-1.0]])]});
            var Q2;
            Q2=makeQuery(id+"F7.imprint","IMPRINT",FACE,{"disambiguationData":[TD([[makeQuery(id+"F7.imprint","IMPRINT",EDGE,{"derivedFrom":sQuery(id+"F7.wireOp",EDGE,"E89.bottom")}),-1.0]])]});
            var Q3;
            Q3=makeQuery(id+"F7.imprint","IMPRINT",FACE,{"disambiguationData":[TD([[makeQuery(id+"F7.imprint","IMPRINT",EDGE,{"derivedFrom":sQuery(id+"F7.wireOp",EDGE,"E88.bottom")}),-1.0]])]});
            var Q4;
            Q4=makeQuery(id+"F5.opExtrude","CAP_FACE",FACE,{"disambiguationData":[OSD([sQuery(id+"F4.wireOp",EDGE,"E32.bottom"),sQuery(id+"F4.wireOp",EDGE,"E32.top"),sQuery(id+"F4.wireOp",EDGE,"E32.left"),sQuery(id+"F4.wireOp",EDGE,"E32.right")])],"isStart":false});
            extrude(context, id + "F8", {"entities" : qUnion([Q0, Q1, Q2, Q3]), "operationType" : NewBodyOperationType.REMOVE, "endBound" : BoundingType.UP_TO_SURFACE, "oppositeDirection" : true, "endBoundEntityFace" : qUnion([Q4]), "depth" : 25.4 * mm});
        }
        {
            var Q0;
            Q0=makeQuery(id+"F3.opExtrude","CAP_FACE",FACE,{"disambiguationData":[OSD([sQuery(id+"F2.wireOp",EDGE,"E22.MirrorCS"),sQuery(id+"F2.wireOp",EDGE,"E23.MirrorCS"),sQuery(id+"F2.wireOp",EDGE,"E24.MirrorCS"),sQuery(id+"F2.wireOp",EDGE,"E25.MirrorCS"),sQuery(id+"F2.wireOp",EDGE,"E30"),sQuery(id+"F2.wireOp",EDGE,"E31")])],"isStart":false});
            var sketch = newSketch(context, id + "F9", { "sketchPlane" : qUnion([Q0])});
            skLineSegment(sketch, "E98.bottom", {"start": v(133.88, -101.6) * mm, "end": v(140.23, -101.6) * mm});
            skLineSegment(sketch, "E98.top", {"start": v(133.88, -104.65) * mm, "end": v(140.23, -104.65) * mm});
            skLineSegment(sketch, "E98.left", {"start": v(133.88, -101.6) * mm, "end": v(133.88, -104.65) * mm});
            skLineSegment(sketch, "E98.right", {"start": v(140.23, -101.6) * mm, "end": v(140.23, -104.65) * mm});
            skLineSegment(sketch, "E99.bottom", {"start": v(155.06, -84.65) * mm, "end": v(158.1, -84.65) * mm});
            skLineSegment(sketch, "E99.top", {"start": v(155.06, -78.3) * mm, "end": v(158.1, -78.3) * mm});
            skLineSegment(sketch, "E99.left", {"start": v(155.06, -84.65) * mm, "end": v(155.06, -78.3) * mm});
            skLineSegment(sketch, "E99.right", {"start": v(158.1, -84.65) * mm, "end": v(158.1, -78.3) * mm});
            skLineSegment(sketch, "E100.MirrorCS", {"start": v(140.23, 28.4) * mm, "end": v(140.23, 31.45) * mm});
            skLineSegment(sketch, "E101.MirrorCS", {"start": v(133.88, 31.45) * mm, "end": v(140.23, 31.45) * mm});
            skLineSegment(sketch, "E102.MirrorCS", {"start": v(133.88, 28.4) * mm, "end": v(133.88, 31.45) * mm});
            skLineSegment(sketch, "E103.MirrorCS", {"start": v(133.88, 28.4) * mm, "end": v(140.23, 28.4) * mm});
            skLineSegment(sketch, "E104.bottom", {"start": v(155.06, 23.32) * mm, "end": v(158.1, 23.32) * mm});
            skLineSegment(sketch, "E104.top", {"start": v(155.06, -9.7) * mm, "end": v(158.1, -9.7) * mm});
            skLineSegment(sketch, "E104.left", {"start": v(155.06, 23.32) * mm, "end": v(155.06, -9.7) * mm});
            skLineSegment(sketch, "E104.right", {"start": v(158.1, 23.32) * mm, "end": v(158.1, -9.7) * mm});
            skSolve(sketch);
        }
        {
            var Q0;
            Q0=makeQuery(id+"F9.imprint","IMPRINT",FACE,{"disambiguationData":[TD([[makeQuery(id+"F9.imprint","IMPRINT",EDGE,{"derivedFrom":sQuery(id+"F9.wireOp",EDGE,"E100.MirrorCS")}),1.0]])]});
            var Q1;
            Q1=makeQuery(id+"F9.imprint","IMPRINT",FACE,{"disambiguationData":[TD([[makeQuery(id+"F9.imprint","IMPRINT",EDGE,{"derivedFrom":sQuery(id+"F9.wireOp",EDGE,"E104.bottom")}),-1.0]])]});
            var Q2;
            Q2=makeQuery(id+"F9.imprint","IMPRINT",FACE,{"disambiguationData":[TD([[makeQuery(id+"F9.imprint","IMPRINT",EDGE,{"derivedFrom":sQuery(id+"F9.wireOp",EDGE,"E99.bottom")}),1.0]])]});
            var Q3;
            Q3=makeQuery(id+"F9.imprint","IMPRINT",FACE,{"disambiguationData":[TD([[makeQuery(id+"F9.imprint","IMPRINT",EDGE,{"derivedFrom":sQuery(id+"F9.wireOp",EDGE,"E98.bottom")}),-1.0]])]});
            var Q4;
            Q4=makeQuery(id+"F5.opExtrude","CAP_FACE",FACE,{"disambiguationData":[OSD([sQuery(id+"F4.wireOp",EDGE,"E36.MirrorCS"),sQuery(id+"F4.wireOp",EDGE,"E37.MirrorCS"),sQuery(id+"F4.wireOp",EDGE,"E38.MirrorCS"),sQuery(id+"F4.wireOp",EDGE,"E39.MirrorCS")])],"isStart":false});
            extrude(context, id + "F10", {"entities" : qUnion([Q0, Q1, Q2, Q3]), "operationType" : NewBodyOperationType.REMOVE, "endBound" : BoundingType.UP_TO_SURFACE, "oppositeDirection" : true, "endBoundEntityFace" : qUnion([Q4]), "depth" : 25.4 * mm});
        }
        {
            var Q0;
            {var subQ0=sQuery(id+"F4.wireOp",EDGE,"E32.right");var subQ1=sQuery(id+"F4.wireOp",EDGE,"E32.left");var subQ2=sQuery(id+"F4.wireOp",EDGE,"E32.top");var subQ3=sQuery(id+"F4.wireOp",EDGE,"E32.bottom");Q0=makeQuery(id+"F8.boolean.opBoolean","MERGE",FACE,{"derivedFrom":[makeQuery(id+"F5.opExtrude","CAP_FACE",FACE,{"disambiguationData":[OSD([subQ3,subQ2,subQ1,subQ0])],"isStart":false}),makeQuery(id+"F8.opExtrude","CAP_FACE",FACE,{"disambiguationData":[OSD([subQ3,subQ2,subQ1,subQ0]),ownerDisambiguation([makeQuery(id+"F8.opExtrude","SWEPT_BODY",BODY,{"disambiguationData":[OSD([sQuery(id+"F7.wireOp",EDGE,"E90.MirrorCS"),sQuery(id+"F7.wireOp",EDGE,"E91.MirrorCS"),sQuery(id+"F7.wireOp",EDGE,"E92.MirrorCS"),sQuery(id+"F7.wireOp",EDGE,"E93.MirrorCS")])]})])],"isStart":false}),makeQuery(id+"F8.opExtrude","CAP_FACE",FACE,{"disambiguationData":[OSD([subQ3,subQ2,subQ1,subQ0]),ownerDisambiguation([makeQuery(id+"F8.opExtrude","SWEPT_BODY",BODY,{"disambiguationData":[OSD([sQuery(id+"F7.wireOp",EDGE,"E94.MirrorCS"),sQuery(id+"F7.wireOp",EDGE,"E95.MirrorCS"),sQuery(id+"F7.wireOp",EDGE,"E96.MirrorCS"),sQuery(id+"F7.wireOp",EDGE,"E97.MirrorCS")])]})])],"isStart":false})]});}
            var sketch = newSketch(context, id + "F11", { "sketchPlane" : qUnion([Q0])});
            skText(sketch, "E105", { "text": "1", "fontName": "OpenSans-Bold.ttf"});
            skText(sketch, "E106", { "text": "2", "fontName": "OpenSans-Bold.ttf"});
            skText(sketch, "E107", { "text": "3", "fontName": "OpenSans-Bold.ttf"});
            const initialGuessF11  = {"E105": [-0.14224, -0.0889, 1, 0, 0.0127], "E106": [-0.14224, 0, 1, 0, 0.0127], "E107": [0.13183, 0.003, 1, 0, 0.0127]};
            skSetInitialGuess(sketch, initialGuessF11);
            skSolve(sketch);
        }
        {
            var Q0;
            Q0 = qSketchRegion(id + "F11", true);
            extrude(context, id + "F12", {"entities" : qUnion([Q0]), "operationType" : NewBodyOperationType.REMOVE, "oppositeDirection" : true, "depth" : 2.54 * mm});
        }
    });
